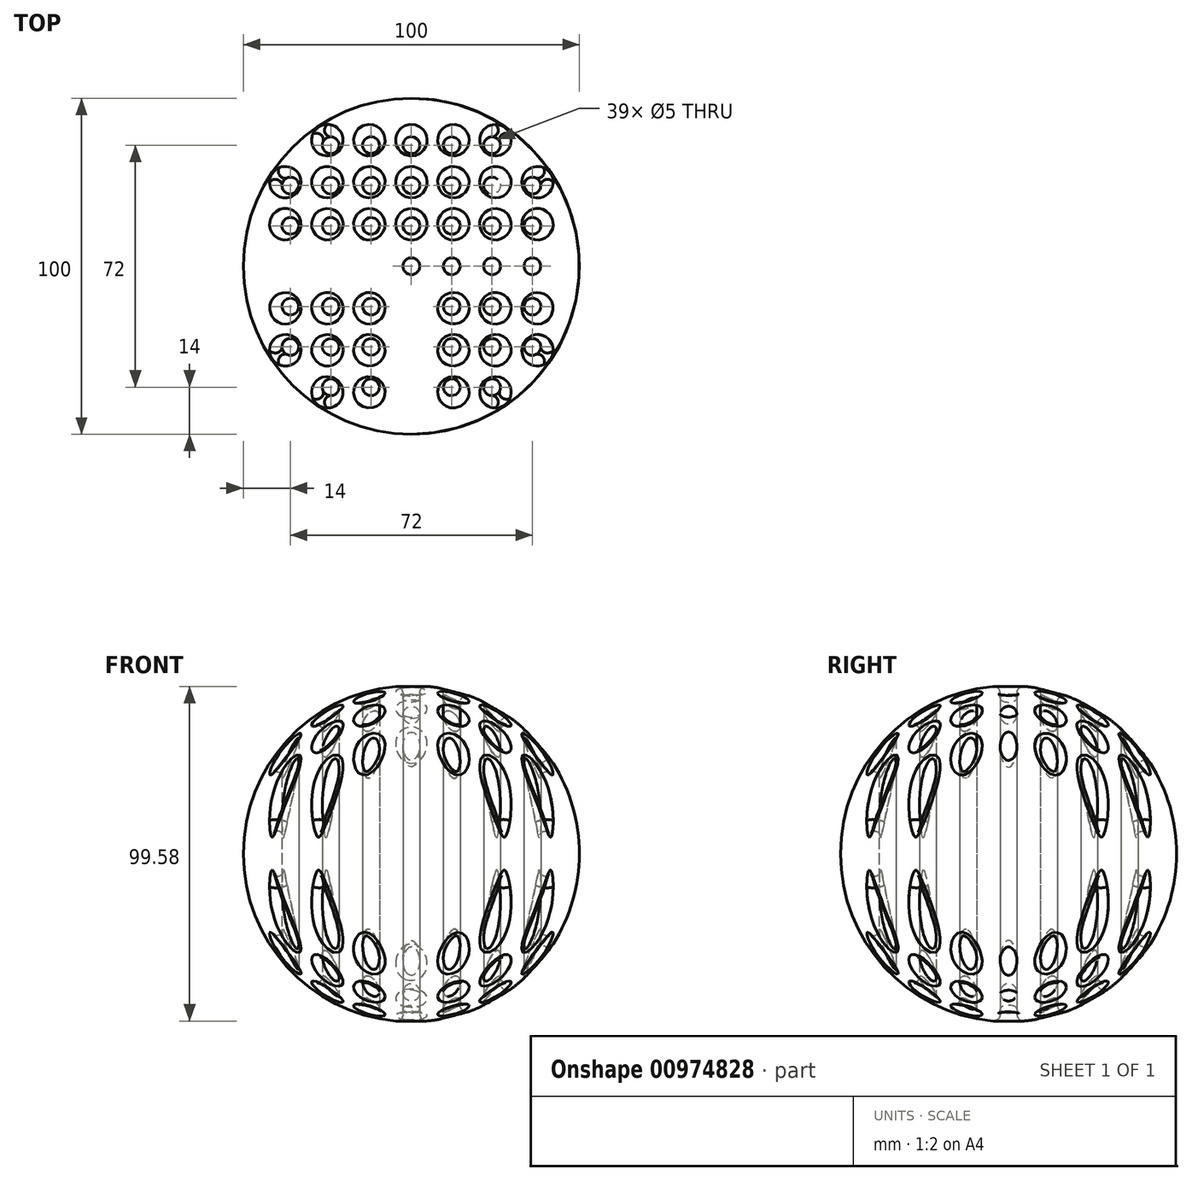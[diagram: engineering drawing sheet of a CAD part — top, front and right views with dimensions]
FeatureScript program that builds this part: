
annotation { "Feature Type Name" : "Feature", "Feature Type Description" : "" }
export const myFeature = defineFeature(function(context is Context, id is Id, definition is map)
    precondition{}
    {
        {
            var Q0;
            Q0=qCreatedBy(makeId("Top.planeOp"),FACE);
            var sketch = newSketch(context, id + "F0", { "sketchPlane" : qUnion([Q0])});
            skCircle(sketch, "E0", {"center": v(0, 0) * mm, "radius": 50 * mm});
            skLineSegment(sketch, "E1", {"start": v(0, 50) * mm, "end": v(0, 0) * mm});
            skLineSegment(sketch, "E2", {"start": v(0, 0) * mm, "end": v(0, -50) * mm});
            skSolve(sketch);
        }
        {
            var Q0;
            {var subQ0=sQuery(id+"F0.wireOp",EDGE,"E1");Q0=makeQuery(id+"F0.imprint","IMPRINT",FACE,{"disambiguationData":[TD([[makeQuery(id+"F0.imprint","IMPRINT",EDGE,{"derivedFrom":subQ0}),1.0]])]});}
            var Q1;
            Q1=sQuery(id+"F0.wireOp",EDGE,"E1");
            revolve(context, id + "F1", {"surfaceOperationType" : NewSurfaceOperationType.NEW, "entities" : qUnion([Q0]), "axis" : qUnion([Q1]), "revolveType" : RevolveType.FULL});
        }
        {
            var Q0;
            Q0=qCreatedBy(makeId("Top.planeOp"),FACE);
            var sketch = newSketch(context, id + "F2", { "sketchPlane" : qUnion([Q0])});
            skCircle(sketch, "E3", {"center": v(0, 0) * mm, "radius": 2.5 * mm});
            skCircle(sketch, "E4", {"center": v(0, 0) * mm, "radius": 50 * mm, "construction": true});
            skCircle(sketch, "E5.0.1.0", {"center": v(0, 12) * mm, "radius": 2.5 * mm});
            skCircle(sketch, "E5.0.2.0", {"center": v(0, 24) * mm, "radius": 2.5 * mm});
            skCircle(sketch, "E5.0.3.0", {"center": v(0, 36) * mm, "radius": 2.5 * mm});
            skCircle(sketch, "E5.1.0.0", {"center": v(12, 0) * mm, "radius": 2.5 * mm});
            skCircle(sketch, "E5.1.1.0", {"center": v(12, 12) * mm, "radius": 2.5 * mm});
            skCircle(sketch, "E5.1.2.0", {"center": v(12, 24) * mm, "radius": 2.5 * mm});
            skCircle(sketch, "E5.1.3.0", {"center": v(12, 36) * mm, "radius": 2.5 * mm});
            skCircle(sketch, "E5.2.0.0", {"center": v(24, 0) * mm, "radius": 2.5 * mm});
            skCircle(sketch, "E5.2.1.0", {"center": v(24, 12) * mm, "radius": 2.5 * mm});
            skCircle(sketch, "E5.2.2.0", {"center": v(24, 24) * mm, "radius": 2.5 * mm});
            skCircle(sketch, "E5.2.3.0", {"center": v(24, 36) * mm, "radius": 2.5 * mm});
            skCircle(sketch, "E5.3.0.0", {"center": v(36, 0) * mm, "radius": 2.5 * mm});
            skCircle(sketch, "E5.3.1.0", {"center": v(36, 12) * mm, "radius": 2.5 * mm});
            skCircle(sketch, "E5.3.2.0", {"center": v(36, 24) * mm, "radius": 2.5 * mm});
            skLineSegment(sketch, "E5.direction1", {"start": v(0, 0) * mm, "end": v(12, 0) * mm, "construction": true});
            skLineSegment(sketch, "E5.direction2", {"start": v(0, 0) * mm, "end": v(0, 12) * mm, "construction": true});
            skCircle(sketch, "E6.1.0", {"center": v(-12, 36) * mm, "radius": 2.5 * mm});
            skCircle(sketch, "E6.1.2", {"center": v(-24, 36) * mm, "radius": 2.5 * mm});
            skCircle(sketch, "E6.1.3", {"center": v(-12, 12) * mm, "radius": 2.5 * mm});
            skLineSegment(sketch, "E6.1.4", {"start": v(0, 0) * mm, "end": v(-12, 0) * mm, "construction": true});
            skCircle(sketch, "E6.1.5", {"center": v(-36, 12) * mm, "radius": 2.5 * mm});
            skCircle(sketch, "E6.1.6", {"center": v(-24, 12) * mm, "radius": 2.5 * mm});
            skCircle(sketch, "E6.1.8", {"center": v(-36, 0) * mm, "radius": 2.5 * mm});
            skCircle(sketch, "E6.1.9", {"center": v(-24, 24) * mm, "radius": 2.5 * mm});
            skCircle(sketch, "E6.1.10", {"center": v(-12, 24) * mm, "radius": 2.5 * mm});
            skCircle(sketch, "E6.1.12", {"center": v(-12, 0) * mm, "radius": 2.5 * mm});
            skCircle(sketch, "E6.1.13", {"center": v(-24, 0) * mm, "radius": 2.5 * mm});
            skCircle(sketch, "E6.1.15", {"center": v(-36, 24) * mm, "radius": 2.5 * mm});
            skCircle(sketch, "E6.2.0", {"center": v(-36, -12) * mm, "radius": 2.5 * mm});
            skCircle(sketch, "E6.2.1", {"center": v(-12, 0) * mm, "radius": 2.5 * mm});
            skCircle(sketch, "E6.2.2", {"center": v(-36, -24) * mm, "radius": 2.5 * mm});
            skCircle(sketch, "E6.2.3", {"center": v(-12, -12) * mm, "radius": 2.5 * mm});
            skLineSegment(sketch, "E6.2.4", {"start": v(0, 0) * mm, "end": v(0, -12) * mm, "construction": true});
            skCircle(sketch, "E6.2.5", {"center": v(-12, -36) * mm, "radius": 2.5 * mm});
            skCircle(sketch, "E6.2.6", {"center": v(-12, -24) * mm, "radius": 2.5 * mm});
            skCircle(sketch, "E6.2.8", {"center": v(0, -36) * mm, "radius": 2.5 * mm});
            skCircle(sketch, "E6.2.9", {"center": v(-24, -24) * mm, "radius": 2.5 * mm});
            skCircle(sketch, "E6.2.10", {"center": v(-24, -12) * mm, "radius": 2.5 * mm});
            skLineSegment(sketch, "E6.2.11", {"start": v(0, 0) * mm, "end": v(-12, 0) * mm, "construction": true});
            skCircle(sketch, "E6.2.12", {"center": v(0, -12) * mm, "radius": 2.5 * mm});
            skCircle(sketch, "E6.2.13", {"center": v(0, -24) * mm, "radius": 2.5 * mm});
            skCircle(sketch, "E6.2.14", {"center": v(-24, 0) * mm, "radius": 2.5 * mm});
            skCircle(sketch, "E6.2.15", {"center": v(-24, -36) * mm, "radius": 2.5 * mm});
            skCircle(sketch, "E6.2.16", {"center": v(-36, 0) * mm, "radius": 2.5 * mm});
            skCircle(sketch, "E6.3.0", {"center": v(12, -36) * mm, "radius": 2.5 * mm});
            skCircle(sketch, "E6.3.1", {"center": v(0, -12) * mm, "radius": 2.5 * mm});
            skCircle(sketch, "E6.3.2", {"center": v(24, -36) * mm, "radius": 2.5 * mm});
            skCircle(sketch, "E6.3.3", {"center": v(12, -12) * mm, "radius": 2.5 * mm});
            skCircle(sketch, "E6.3.5", {"center": v(36, -12) * mm, "radius": 2.5 * mm});
            skCircle(sketch, "E6.3.6", {"center": v(24, -12) * mm, "radius": 2.5 * mm});
            skCircle(sketch, "E6.3.9", {"center": v(24, -24) * mm, "radius": 2.5 * mm});
            skCircle(sketch, "E6.3.10", {"center": v(12, -24) * mm, "radius": 2.5 * mm});
            skLineSegment(sketch, "E6.3.11", {"start": v(0, 0) * mm, "end": v(0, -12) * mm, "construction": true});
            skCircle(sketch, "E6.3.14", {"center": v(0, -24) * mm, "radius": 2.5 * mm});
            skCircle(sketch, "E6.3.15", {"center": v(36, -24) * mm, "radius": 2.5 * mm});
            skCircle(sketch, "E6.3.16", {"center": v(0, -36) * mm, "radius": 2.5 * mm});
            skSolve(sketch);
        }
        {
            var Q0;
            Q0=makeQuery(id+"F2.imprint","IMPRINT",FACE,{"disambiguationData":[TD([[makeQuery(id+"F2.imprint","IMPRINT",EDGE,{"derivedFrom":sQuery(id+"F2.wireOp",EDGE,"E6.1.2")}),1.0]])]});
            var Q1;
            Q1=makeQuery(id+"F2.imprint","IMPRINT",FACE,{"disambiguationData":[TD([[makeQuery(id+"F2.imprint","IMPRINT",EDGE,{"derivedFrom":sQuery(id+"F2.wireOp",EDGE,"E6.1.0")}),1.0]])]});
            var Q2;
            Q2=makeQuery(id+"F2.imprint","IMPRINT",FACE,{"disambiguationData":[TD([[makeQuery(id+"F2.imprint","IMPRINT",EDGE,{"derivedFrom":sQuery(id+"F2.wireOp",EDGE,"E5.0.3.0")}),1.0]])]});
            var Q3;
            Q3=makeQuery(id+"F2.imprint","IMPRINT",FACE,{"disambiguationData":[TD([[makeQuery(id+"F2.imprint","IMPRINT",EDGE,{"derivedFrom":sQuery(id+"F2.wireOp",EDGE,"E5.1.3.0")}),1.0]])]});
            var Q4;
            Q4=makeQuery(id+"F2.imprint","IMPRINT",FACE,{"disambiguationData":[TD([[makeQuery(id+"F2.imprint","IMPRINT",EDGE,{"derivedFrom":sQuery(id+"F2.wireOp",EDGE,"E5.2.3.0")}),1.0]])]});
            var Q5;
            Q5=makeQuery(id+"F2.imprint","IMPRINT",FACE,{"disambiguationData":[TD([[makeQuery(id+"F2.imprint","IMPRINT",EDGE,{"derivedFrom":sQuery(id+"F2.wireOp",EDGE,"E5.2.2.0")}),1.0]])]});
            var Q6;
            Q6=makeQuery(id+"F2.imprint","IMPRINT",FACE,{"disambiguationData":[TD([[makeQuery(id+"F2.imprint","IMPRINT",EDGE,{"derivedFrom":sQuery(id+"F2.wireOp",EDGE,"E5.3.2.0")}),1.0]])]});
            var Q7;
            Q7=makeQuery(id+"F2.imprint","IMPRINT",FACE,{"disambiguationData":[TD([[makeQuery(id+"F2.imprint","IMPRINT",EDGE,{"derivedFrom":sQuery(id+"F2.wireOp",EDGE,"E5.1.2.0")}),1.0]])]});
            var Q8;
            Q8=makeQuery(id+"F2.imprint","IMPRINT",FACE,{"disambiguationData":[TD([[makeQuery(id+"F2.imprint","IMPRINT",EDGE,{"derivedFrom":sQuery(id+"F2.wireOp",EDGE,"E5.0.2.0")}),1.0]])]});
            var Q9;
            Q9=makeQuery(id+"F2.imprint","IMPRINT",FACE,{"disambiguationData":[TD([[makeQuery(id+"F2.imprint","IMPRINT",EDGE,{"derivedFrom":sQuery(id+"F2.wireOp",EDGE,"E6.1.10")}),1.0]])]});
            var Q10;
            Q10=makeQuery(id+"F2.imprint","IMPRINT",FACE,{"disambiguationData":[TD([[makeQuery(id+"F2.imprint","IMPRINT",EDGE,{"derivedFrom":sQuery(id+"F2.wireOp",EDGE,"E6.1.9")}),1.0]])]});
            var Q11;
            Q11=makeQuery(id+"F2.imprint","IMPRINT",FACE,{"disambiguationData":[TD([[makeQuery(id+"F2.imprint","IMPRINT",EDGE,{"derivedFrom":sQuery(id+"F2.wireOp",EDGE,"E6.1.15")}),1.0]])]});
            var Q12;
            Q12=makeQuery(id+"F2.imprint","IMPRINT",FACE,{"disambiguationData":[TD([[makeQuery(id+"F2.imprint","IMPRINT",EDGE,{"derivedFrom":sQuery(id+"F2.wireOp",EDGE,"E6.1.5")}),1.0]])]});
            var Q13;
            Q13=makeQuery(id+"F2.imprint","IMPRINT",FACE,{"disambiguationData":[TD([[makeQuery(id+"F2.imprint","IMPRINT",EDGE,{"derivedFrom":sQuery(id+"F2.wireOp",EDGE,"E6.1.6")}),1.0]])]});
            var Q14;
            Q14=makeQuery(id+"F2.imprint","IMPRINT",FACE,{"disambiguationData":[TD([[makeQuery(id+"F2.imprint","IMPRINT",EDGE,{"derivedFrom":sQuery(id+"F2.wireOp",EDGE,"E6.1.3")}),1.0]])]});
            var Q15;
            Q15=makeQuery(id+"F2.imprint","IMPRINT",FACE,{"disambiguationData":[TD([[makeQuery(id+"F2.imprint","IMPRINT",EDGE,{"derivedFrom":sQuery(id+"F2.wireOp",EDGE,"E5.0.1.0")}),1.0]])]});
            var Q16;
            Q16=makeQuery(id+"F2.imprint","IMPRINT",FACE,{"disambiguationData":[TD([[makeQuery(id+"F2.imprint","IMPRINT",EDGE,{"derivedFrom":sQuery(id+"F2.wireOp",EDGE,"E5.1.1.0")}),1.0]])]});
            var Q17;
            Q17=makeQuery(id+"F2.imprint","IMPRINT",FACE,{"disambiguationData":[TD([[makeQuery(id+"F2.imprint","IMPRINT",EDGE,{"derivedFrom":sQuery(id+"F2.wireOp",EDGE,"E5.2.1.0")}),1.0]])]});
            var Q18;
            Q18=makeQuery(id+"F2.imprint","IMPRINT",FACE,{"disambiguationData":[TD([[makeQuery(id+"F2.imprint","IMPRINT",EDGE,{"derivedFrom":sQuery(id+"F2.wireOp",EDGE,"E5.3.1.0")}),1.0]])]});
            var Q19;
            Q19=makeQuery(id+"F2.imprint","IMPRINT",FACE,{"disambiguationData":[TD([[makeQuery(id+"F2.imprint","IMPRINT",EDGE,{"derivedFrom":sQuery(id+"F2.wireOp",EDGE,"E5.3.0.0")}),1.0]])]});
            var Q20;
            Q20=makeQuery(id+"F2.imprint","IMPRINT",FACE,{"disambiguationData":[TD([[makeQuery(id+"F2.imprint","IMPRINT",EDGE,{"derivedFrom":sQuery(id+"F2.wireOp",EDGE,"E5.2.0.0")}),1.0]])]});
            var Q21;
            Q21=makeQuery(id+"F2.imprint","IMPRINT",FACE,{"disambiguationData":[TD([[makeQuery(id+"F2.imprint","IMPRINT",EDGE,{"derivedFrom":sQuery(id+"F2.wireOp",EDGE,"E5.1.0.0")}),1.0]])]});
            var Q22;
            Q22=makeQuery(id+"F2.imprint","IMPRINT",FACE,{"disambiguationData":[TD([[makeQuery(id+"F2.imprint","IMPRINT",EDGE,{"derivedFrom":sQuery(id+"F2.wireOp",EDGE,"E3")}),1.0]])]});
            var Q23;
            Q23=makeQuery(id+"F2.imprint","IMPRINT",FACE,{"disambiguationData":[TD([[makeQuery(id+"F2.imprint","IMPRINT",EDGE,{"derivedFrom":sQuery(id+"F2.wireOp",EDGE,"E6.2.1")}),1.0]])]});
            var Q24;
            Q24=makeQuery(id+"F2.imprint","IMPRINT",FACE,{"disambiguationData":[TD([[makeQuery(id+"F2.imprint","IMPRINT",EDGE,{"derivedFrom":sQuery(id+"F2.wireOp",EDGE,"E6.2.14")}),1.0]])]});
            var Q25;
            Q25=makeQuery(id+"F2.imprint","IMPRINT",FACE,{"disambiguationData":[TD([[makeQuery(id+"F2.imprint","IMPRINT",EDGE,{"derivedFrom":sQuery(id+"F2.wireOp",EDGE,"E6.2.16")}),1.0]])]});
            var Q26;
            Q26=makeQuery(id+"F2.imprint","IMPRINT",FACE,{"disambiguationData":[TD([[makeQuery(id+"F2.imprint","IMPRINT",EDGE,{"derivedFrom":sQuery(id+"F2.wireOp",EDGE,"E6.2.0")}),1.0]])]});
            var Q27;
            Q27=makeQuery(id+"F2.imprint","IMPRINT",FACE,{"disambiguationData":[TD([[makeQuery(id+"F2.imprint","IMPRINT",EDGE,{"derivedFrom":sQuery(id+"F2.wireOp",EDGE,"E6.2.10")}),1.0]])]});
            var Q28;
            Q28=makeQuery(id+"F2.imprint","IMPRINT",FACE,{"disambiguationData":[TD([[makeQuery(id+"F2.imprint","IMPRINT",EDGE,{"derivedFrom":sQuery(id+"F2.wireOp",EDGE,"E6.2.3")}),1.0]])]});
            var Q29;
            Q29=makeQuery(id+"F2.imprint","IMPRINT",FACE,{"disambiguationData":[TD([[makeQuery(id+"F2.imprint","IMPRINT",EDGE,{"derivedFrom":sQuery(id+"F2.wireOp",EDGE,"E6.3.1")}),1.0]])]});
            var Q30;
            Q30=makeQuery(id+"F2.imprint","IMPRINT",FACE,{"disambiguationData":[TD([[makeQuery(id+"F2.imprint","IMPRINT",EDGE,{"derivedFrom":sQuery(id+"F2.wireOp",EDGE,"E6.3.3")}),1.0]])]});
            var Q31;
            Q31=makeQuery(id+"F2.imprint","IMPRINT",FACE,{"disambiguationData":[TD([[makeQuery(id+"F2.imprint","IMPRINT",EDGE,{"derivedFrom":sQuery(id+"F2.wireOp",EDGE,"E6.3.6")}),1.0]])]});
            var Q32;
            Q32=makeQuery(id+"F2.imprint","IMPRINT",FACE,{"disambiguationData":[TD([[makeQuery(id+"F2.imprint","IMPRINT",EDGE,{"derivedFrom":sQuery(id+"F2.wireOp",EDGE,"E6.3.5")}),1.0]])]});
            var Q33;
            Q33=makeQuery(id+"F2.imprint","IMPRINT",FACE,{"disambiguationData":[TD([[makeQuery(id+"F2.imprint","IMPRINT",EDGE,{"derivedFrom":sQuery(id+"F2.wireOp",EDGE,"E6.2.2")}),1.0]])]});
            var Q34;
            Q34=makeQuery(id+"F2.imprint","IMPRINT",FACE,{"disambiguationData":[TD([[makeQuery(id+"F2.imprint","IMPRINT",EDGE,{"derivedFrom":sQuery(id+"F2.wireOp",EDGE,"E6.2.9")}),1.0]])]});
            var Q35;
            Q35=makeQuery(id+"F2.imprint","IMPRINT",FACE,{"disambiguationData":[TD([[makeQuery(id+"F2.imprint","IMPRINT",EDGE,{"derivedFrom":sQuery(id+"F2.wireOp",EDGE,"E6.2.6")}),1.0]])]});
            var Q36;
            Q36=makeQuery(id+"F2.imprint","IMPRINT",FACE,{"disambiguationData":[TD([[makeQuery(id+"F2.imprint","IMPRINT",EDGE,{"derivedFrom":sQuery(id+"F2.wireOp",EDGE,"E6.3.14")}),1.0]])]});
            var Q37;
            Q37=makeQuery(id+"F2.imprint","IMPRINT",FACE,{"disambiguationData":[TD([[makeQuery(id+"F2.imprint","IMPRINT",EDGE,{"derivedFrom":sQuery(id+"F2.wireOp",EDGE,"E6.3.10")}),1.0]])]});
            var Q38;
            Q38=makeQuery(id+"F2.imprint","IMPRINT",FACE,{"disambiguationData":[TD([[makeQuery(id+"F2.imprint","IMPRINT",EDGE,{"derivedFrom":sQuery(id+"F2.wireOp",EDGE,"E6.3.9")}),1.0]])]});
            var Q39;
            Q39=makeQuery(id+"F2.imprint","IMPRINT",FACE,{"disambiguationData":[TD([[makeQuery(id+"F2.imprint","IMPRINT",EDGE,{"derivedFrom":sQuery(id+"F2.wireOp",EDGE,"E6.3.15")}),1.0]])]});
            var Q40;
            Q40=makeQuery(id+"F2.imprint","IMPRINT",FACE,{"disambiguationData":[TD([[makeQuery(id+"F2.imprint","IMPRINT",EDGE,{"derivedFrom":sQuery(id+"F2.wireOp",EDGE,"E6.3.2")}),1.0]])]});
            var Q41;
            Q41=makeQuery(id+"F2.imprint","IMPRINT",FACE,{"disambiguationData":[TD([[makeQuery(id+"F2.imprint","IMPRINT",EDGE,{"derivedFrom":sQuery(id+"F2.wireOp",EDGE,"E6.3.0")}),1.0]])]});
            var Q42;
            Q42=makeQuery(id+"F2.imprint","IMPRINT",FACE,{"disambiguationData":[TD([[makeQuery(id+"F2.imprint","IMPRINT",EDGE,{"derivedFrom":sQuery(id+"F2.wireOp",EDGE,"E6.3.16")}),1.0]])]});
            var Q43;
            Q43=makeQuery(id+"F2.imprint","IMPRINT",FACE,{"disambiguationData":[TD([[makeQuery(id+"F2.imprint","IMPRINT",EDGE,{"derivedFrom":sQuery(id+"F2.wireOp",EDGE,"E6.2.5")}),1.0]])]});
            var Q44;
            Q44=makeQuery(id+"F2.imprint","IMPRINT",FACE,{"disambiguationData":[TD([[makeQuery(id+"F2.imprint","IMPRINT",EDGE,{"derivedFrom":sQuery(id+"F2.wireOp",EDGE,"E6.2.15")}),1.0]])]});
            extrude(context, id + "F3", {"entities" : qUnion([Q0, Q1, Q2, Q3, Q4, Q5, Q6, Q7, Q8, Q9, Q10, Q11, Q12, Q13, Q14, Q15, Q16, Q17, Q18, Q19, Q20, Q21, Q22, Q23, Q24, Q25, Q26, Q27, Q28, Q29, Q30, Q31, Q32, Q33, Q34, Q35, Q36, Q37, Q38, Q39, Q40, Q41, Q42, Q43, Q44]), "operationType" : NewBodyOperationType.REMOVE, "endBound" : BoundingType.SYMMETRIC, "depth" : 179 * mm, "offsetDistance" : 25 * mm});
        }
        {
            var Q0;
            Q0=makeQuery(id+"F3.boolean.opBoolean","INTERSECT",EDGE,{"disambiguationData":[OD(1.0)],"derivedFrom":[makeQuery(id+"F1.opRevolve","SWEPT_FACE",FACE,{"disambiguationData":[OSD([sQuery(id+"F0.wireOp",EDGE,"E0")])]}),makeQuery(id+"F3.opExtrude","SWEPT_FACE",FACE,{"disambiguationData":[OSD([sQuery(id+"F2.wireOp",EDGE,"E6.2.16")])]})]});
            var Q1;
            Q1=makeQuery(id+"F3.boolean.opBoolean","INTERSECT",EDGE,{"disambiguationData":[OD(1.0)],"derivedFrom":[makeQuery(id+"F1.opRevolve","SWEPT_FACE",FACE,{"disambiguationData":[OSD([sQuery(id+"F0.wireOp",EDGE,"E0")])]}),makeQuery(id+"F3.opExtrude","SWEPT_FACE",FACE,{"disambiguationData":[OSD([sQuery(id+"F2.wireOp",EDGE,"E6.2.2")])]})]});
            var Q2;
            Q2=makeQuery(id+"F3.boolean.opBoolean","INTERSECT",EDGE,{"disambiguationData":[OD(1.0)],"derivedFrom":[makeQuery(id+"F1.opRevolve","SWEPT_FACE",FACE,{"disambiguationData":[OSD([sQuery(id+"F0.wireOp",EDGE,"E0")])]}),makeQuery(id+"F3.opExtrude","SWEPT_FACE",FACE,{"disambiguationData":[OSD([sQuery(id+"F2.wireOp",EDGE,"E6.1.6")])]})]});
            var Q3;
            Q3=makeQuery(id+"F3.boolean.opBoolean","INTERSECT",EDGE,{"disambiguationData":[OD(1.0)],"derivedFrom":[makeQuery(id+"F1.opRevolve","SWEPT_FACE",FACE,{"disambiguationData":[OSD([sQuery(id+"F0.wireOp",EDGE,"E0")])]}),makeQuery(id+"F3.opExtrude","SWEPT_FACE",FACE,{"disambiguationData":[OSD([sQuery(id+"F2.wireOp",EDGE,"E6.3.16")])]})]});
            var Q4;
            Q4=makeQuery(id+"F3.boolean.opBoolean","INTERSECT",EDGE,{"disambiguationData":[OD(1.0)],"derivedFrom":[makeQuery(id+"F1.opRevolve","SWEPT_FACE",FACE,{"disambiguationData":[OSD([sQuery(id+"F0.wireOp",EDGE,"E0")])]}),makeQuery(id+"F3.opExtrude","SWEPT_FACE",FACE,{"disambiguationData":[OSD([sQuery(id+"F2.wireOp",EDGE,"E6.1.5")])]})]});
            var Q5;
            Q5=makeQuery(id+"F3.boolean.opBoolean","INTERSECT",EDGE,{"disambiguationData":[OD(1.0)],"derivedFrom":[makeQuery(id+"F1.opRevolve","SWEPT_FACE",FACE,{"disambiguationData":[OSD([sQuery(id+"F0.wireOp",EDGE,"E0")])]}),makeQuery(id+"F3.opExtrude","SWEPT_FACE",FACE,{"disambiguationData":[OSD([sQuery(id+"F2.wireOp",EDGE,"E6.2.1")])]})]});
            var Q6;
            Q6=makeQuery(id+"F3.boolean.opBoolean","INTERSECT",EDGE,{"disambiguationData":[OD(1.0)],"derivedFrom":[makeQuery(id+"F1.opRevolve","SWEPT_FACE",FACE,{"disambiguationData":[OSD([sQuery(id+"F0.wireOp",EDGE,"E0")])]}),makeQuery(id+"F3.opExtrude","SWEPT_FACE",FACE,{"disambiguationData":[OSD([sQuery(id+"F2.wireOp",EDGE,"E6.1.3")])]})]});
            var Q7;
            Q7=makeQuery(id+"F3.boolean.opBoolean","INTERSECT",EDGE,{"disambiguationData":[OD(1.0)],"derivedFrom":[makeQuery(id+"F1.opRevolve","SWEPT_FACE",FACE,{"disambiguationData":[OSD([sQuery(id+"F0.wireOp",EDGE,"E0")])]}),makeQuery(id+"F3.opExtrude","SWEPT_FACE",FACE,{"disambiguationData":[OSD([sQuery(id+"F2.wireOp",EDGE,"E6.3.14")])]})]});
            var Q8;
            Q8=makeQuery(id+"F3.boolean.opBoolean","INTERSECT",EDGE,{"disambiguationData":[OD(1.0)],"derivedFrom":[makeQuery(id+"F1.opRevolve","SWEPT_FACE",FACE,{"disambiguationData":[OSD([sQuery(id+"F0.wireOp",EDGE,"E0")])]}),makeQuery(id+"F3.opExtrude","SWEPT_FACE",FACE,{"disambiguationData":[OSD([sQuery(id+"F2.wireOp",EDGE,"E6.2.10")])]})]});
            var Q9;
            Q9=makeQuery(id+"F3.boolean.opBoolean","INTERSECT",EDGE,{"disambiguationData":[OD(1.0)],"derivedFrom":[makeQuery(id+"F1.opRevolve","SWEPT_FACE",FACE,{"disambiguationData":[OSD([sQuery(id+"F0.wireOp",EDGE,"E0")])]}),makeQuery(id+"F3.opExtrude","SWEPT_FACE",FACE,{"disambiguationData":[OSD([sQuery(id+"F2.wireOp",EDGE,"E6.3.5")])]})]});
            var Q10;
            Q10=makeQuery(id+"F3.boolean.opBoolean","INTERSECT",EDGE,{"disambiguationData":[OD(1.0)],"derivedFrom":[makeQuery(id+"F1.opRevolve","SWEPT_FACE",FACE,{"disambiguationData":[OSD([sQuery(id+"F0.wireOp",EDGE,"E0")])]}),makeQuery(id+"F3.opExtrude","SWEPT_FACE",FACE,{"disambiguationData":[OSD([sQuery(id+"F2.wireOp",EDGE,"E6.1.2")])]})]});
            var Q11;
            Q11=makeQuery(id+"F3.boolean.opBoolean","INTERSECT",EDGE,{"disambiguationData":[OD(1.0)],"derivedFrom":[makeQuery(id+"F1.opRevolve","SWEPT_FACE",FACE,{"disambiguationData":[OSD([sQuery(id+"F0.wireOp",EDGE,"E0")])]}),makeQuery(id+"F3.opExtrude","SWEPT_FACE",FACE,{"disambiguationData":[OSD([sQuery(id+"F2.wireOp",EDGE,"E5.0.3.0")])]})]});
            var Q12;
            Q12=makeQuery(id+"F3.boolean.opBoolean","INTERSECT",EDGE,{"disambiguationData":[OD(1.0)],"derivedFrom":[makeQuery(id+"F1.opRevolve","SWEPT_FACE",FACE,{"disambiguationData":[OSD([sQuery(id+"F0.wireOp",EDGE,"E0")])]}),makeQuery(id+"F3.opExtrude","SWEPT_FACE",FACE,{"disambiguationData":[OSD([sQuery(id+"F2.wireOp",EDGE,"E6.3.3")])]})]});
            var Q13;
            Q13=makeQuery(id+"F3.boolean.opBoolean","INTERSECT",EDGE,{"disambiguationData":[OD(1.0)],"derivedFrom":[makeQuery(id+"F1.opRevolve","SWEPT_FACE",FACE,{"disambiguationData":[OSD([sQuery(id+"F0.wireOp",EDGE,"E0")])]}),makeQuery(id+"F3.opExtrude","SWEPT_FACE",FACE,{"disambiguationData":[OSD([sQuery(id+"F2.wireOp",EDGE,"E5.2.0.0")])]})]});
            var Q14;
            Q14=makeQuery(id+"F3.boolean.opBoolean","INTERSECT",EDGE,{"disambiguationData":[OD(1.0)],"derivedFrom":[makeQuery(id+"F1.opRevolve","SWEPT_FACE",FACE,{"disambiguationData":[OSD([sQuery(id+"F0.wireOp",EDGE,"E0")])]}),makeQuery(id+"F3.opExtrude","SWEPT_FACE",FACE,{"disambiguationData":[OSD([sQuery(id+"F2.wireOp",EDGE,"E5.1.0.0")])]})]});
            var Q15;
            Q15=makeQuery(id+"F3.boolean.opBoolean","INTERSECT",EDGE,{"disambiguationData":[OD(1.0)],"derivedFrom":[makeQuery(id+"F1.opRevolve","SWEPT_FACE",FACE,{"disambiguationData":[OSD([sQuery(id+"F0.wireOp",EDGE,"E0")])]}),makeQuery(id+"F3.opExtrude","SWEPT_FACE",FACE,{"disambiguationData":[OSD([sQuery(id+"F2.wireOp",EDGE,"E6.2.6")])]})]});
            var Q16;
            Q16=makeQuery(id+"F3.boolean.opBoolean","INTERSECT",EDGE,{"disambiguationData":[OD(1.0)],"derivedFrom":[makeQuery(id+"F1.opRevolve","SWEPT_FACE",FACE,{"disambiguationData":[OSD([sQuery(id+"F0.wireOp",EDGE,"E0")])]}),makeQuery(id+"F3.opExtrude","SWEPT_FACE",FACE,{"disambiguationData":[OSD([sQuery(id+"F2.wireOp",EDGE,"E5.1.1.0")])]})]});
            var Q17;
            Q17=makeQuery(id+"F3.boolean.opBoolean","INTERSECT",EDGE,{"disambiguationData":[OD(1.0)],"derivedFrom":[makeQuery(id+"F1.opRevolve","SWEPT_FACE",FACE,{"disambiguationData":[OSD([sQuery(id+"F0.wireOp",EDGE,"E0")])]}),makeQuery(id+"F3.opExtrude","SWEPT_FACE",FACE,{"disambiguationData":[OSD([sQuery(id+"F2.wireOp",EDGE,"E6.1.9")])]})]});
            var Q18;
            Q18=makeQuery(id+"F3.boolean.opBoolean","INTERSECT",EDGE,{"disambiguationData":[OD(1.0)],"derivedFrom":[makeQuery(id+"F1.opRevolve","SWEPT_FACE",FACE,{"disambiguationData":[OSD([sQuery(id+"F0.wireOp",EDGE,"E0")])]}),makeQuery(id+"F3.opExtrude","SWEPT_FACE",FACE,{"disambiguationData":[OSD([sQuery(id+"F2.wireOp",EDGE,"E6.1.15")])]})]});
            var Q19;
            Q19=makeQuery(id+"F3.boolean.opBoolean","INTERSECT",EDGE,{"disambiguationData":[OD(1.0)],"derivedFrom":[makeQuery(id+"F1.opRevolve","SWEPT_FACE",FACE,{"disambiguationData":[OSD([sQuery(id+"F0.wireOp",EDGE,"E0")])]}),makeQuery(id+"F3.opExtrude","SWEPT_FACE",FACE,{"disambiguationData":[OSD([sQuery(id+"F2.wireOp",EDGE,"E6.2.15")])]})]});
            var Q20;
            Q20=makeQuery(id+"F3.boolean.opBoolean","INTERSECT",EDGE,{"disambiguationData":[OD(1.0)],"derivedFrom":[makeQuery(id+"F1.opRevolve","SWEPT_FACE",FACE,{"disambiguationData":[OSD([sQuery(id+"F0.wireOp",EDGE,"E0")])]}),makeQuery(id+"F3.opExtrude","SWEPT_FACE",FACE,{"disambiguationData":[OSD([sQuery(id+"F2.wireOp",EDGE,"E3")])]})]});
            var Q21;
            Q21=makeQuery(id+"F3.boolean.opBoolean","INTERSECT",EDGE,{"disambiguationData":[OD(1.0)],"derivedFrom":[makeQuery(id+"F1.opRevolve","SWEPT_FACE",FACE,{"disambiguationData":[OSD([sQuery(id+"F0.wireOp",EDGE,"E0")])]}),makeQuery(id+"F3.opExtrude","SWEPT_FACE",FACE,{"disambiguationData":[OSD([sQuery(id+"F2.wireOp",EDGE,"E6.3.1")])]})]});
            var Q22;
            Q22=makeQuery(id+"F3.boolean.opBoolean","INTERSECT",EDGE,{"disambiguationData":[OD(1.0)],"derivedFrom":[makeQuery(id+"F1.opRevolve","SWEPT_FACE",FACE,{"disambiguationData":[OSD([sQuery(id+"F0.wireOp",EDGE,"E0")])]}),makeQuery(id+"F3.opExtrude","SWEPT_FACE",FACE,{"disambiguationData":[OSD([sQuery(id+"F2.wireOp",EDGE,"E5.3.1.0")])]})]});
            var Q23;
            Q23=makeQuery(id+"F3.boolean.opBoolean","INTERSECT",EDGE,{"disambiguationData":[OD(1.0)],"derivedFrom":[makeQuery(id+"F1.opRevolve","SWEPT_FACE",FACE,{"disambiguationData":[OSD([sQuery(id+"F0.wireOp",EDGE,"E0")])]}),makeQuery(id+"F3.opExtrude","SWEPT_FACE",FACE,{"disambiguationData":[OSD([sQuery(id+"F2.wireOp",EDGE,"E5.2.1.0")])]})]});
            var Q24;
            Q24=makeQuery(id+"F3.boolean.opBoolean","INTERSECT",EDGE,{"disambiguationData":[OD(1.0)],"derivedFrom":[makeQuery(id+"F1.opRevolve","SWEPT_FACE",FACE,{"disambiguationData":[OSD([sQuery(id+"F0.wireOp",EDGE,"E0")])]}),makeQuery(id+"F3.opExtrude","SWEPT_FACE",FACE,{"disambiguationData":[OSD([sQuery(id+"F2.wireOp",EDGE,"E6.1.0")])]})]});
            var Q25;
            Q25=makeQuery(id+"F3.boolean.opBoolean","INTERSECT",EDGE,{"disambiguationData":[OD(1.0)],"derivedFrom":[makeQuery(id+"F1.opRevolve","SWEPT_FACE",FACE,{"disambiguationData":[OSD([sQuery(id+"F0.wireOp",EDGE,"E0")])]}),makeQuery(id+"F3.opExtrude","SWEPT_FACE",FACE,{"disambiguationData":[OSD([sQuery(id+"F2.wireOp",EDGE,"E5.0.2.0")])]})]});
            var Q26;
            Q26=makeQuery(id+"F3.boolean.opBoolean","INTERSECT",EDGE,{"disambiguationData":[OD(1.0)],"derivedFrom":[makeQuery(id+"F1.opRevolve","SWEPT_FACE",FACE,{"disambiguationData":[OSD([sQuery(id+"F0.wireOp",EDGE,"E0")])]}),makeQuery(id+"F3.opExtrude","SWEPT_FACE",FACE,{"disambiguationData":[OSD([sQuery(id+"F2.wireOp",EDGE,"E5.3.2.0")])]})]});
            var Q27;
            Q27=makeQuery(id+"F3.boolean.opBoolean","INTERSECT",EDGE,{"disambiguationData":[OD(1.0)],"derivedFrom":[makeQuery(id+"F1.opRevolve","SWEPT_FACE",FACE,{"disambiguationData":[OSD([sQuery(id+"F0.wireOp",EDGE,"E0")])]}),makeQuery(id+"F3.opExtrude","SWEPT_FACE",FACE,{"disambiguationData":[OSD([sQuery(id+"F2.wireOp",EDGE,"E5.0.1.0")])]})]});
            var Q28;
            Q28=makeQuery(id+"F3.boolean.opBoolean","INTERSECT",EDGE,{"disambiguationData":[OD(1.0)],"derivedFrom":[makeQuery(id+"F1.opRevolve","SWEPT_FACE",FACE,{"disambiguationData":[OSD([sQuery(id+"F0.wireOp",EDGE,"E0")])]}),makeQuery(id+"F3.opExtrude","SWEPT_FACE",FACE,{"disambiguationData":[OSD([sQuery(id+"F2.wireOp",EDGE,"E6.3.2")])]})]});
            var Q29;
            Q29=makeQuery(id+"F3.boolean.opBoolean","INTERSECT",EDGE,{"disambiguationData":[OD(1.0)],"derivedFrom":[makeQuery(id+"F1.opRevolve","SWEPT_FACE",FACE,{"disambiguationData":[OSD([sQuery(id+"F0.wireOp",EDGE,"E0")])]}),makeQuery(id+"F3.opExtrude","SWEPT_FACE",FACE,{"disambiguationData":[OSD([sQuery(id+"F2.wireOp",EDGE,"E6.3.6")])]})]});
            var Q30;
            Q30=makeQuery(id+"F3.boolean.opBoolean","INTERSECT",EDGE,{"disambiguationData":[OD(1.0)],"derivedFrom":[makeQuery(id+"F1.opRevolve","SWEPT_FACE",FACE,{"disambiguationData":[OSD([sQuery(id+"F0.wireOp",EDGE,"E0")])]}),makeQuery(id+"F3.opExtrude","SWEPT_FACE",FACE,{"disambiguationData":[OSD([sQuery(id+"F2.wireOp",EDGE,"E5.1.2.0")])]})]});
            var Q31;
            Q31=makeQuery(id+"F3.boolean.opBoolean","INTERSECT",EDGE,{"disambiguationData":[OD(1.0)],"derivedFrom":[makeQuery(id+"F1.opRevolve","SWEPT_FACE",FACE,{"disambiguationData":[OSD([sQuery(id+"F0.wireOp",EDGE,"E0")])]}),makeQuery(id+"F3.opExtrude","SWEPT_FACE",FACE,{"disambiguationData":[OSD([sQuery(id+"F2.wireOp",EDGE,"E5.1.3.0")])]})]});
            var Q32;
            Q32=makeQuery(id+"F3.boolean.opBoolean","INTERSECT",EDGE,{"disambiguationData":[OD(1.0)],"derivedFrom":[makeQuery(id+"F1.opRevolve","SWEPT_FACE",FACE,{"disambiguationData":[OSD([sQuery(id+"F0.wireOp",EDGE,"E0")])]}),makeQuery(id+"F3.opExtrude","SWEPT_FACE",FACE,{"disambiguationData":[OSD([sQuery(id+"F2.wireOp",EDGE,"E6.2.3")])]})]});
            var Q33;
            Q33=makeQuery(id+"F3.boolean.opBoolean","INTERSECT",EDGE,{"disambiguationData":[OD(1.0)],"derivedFrom":[makeQuery(id+"F1.opRevolve","SWEPT_FACE",FACE,{"disambiguationData":[OSD([sQuery(id+"F0.wireOp",EDGE,"E0")])]}),makeQuery(id+"F3.opExtrude","SWEPT_FACE",FACE,{"disambiguationData":[OSD([sQuery(id+"F2.wireOp",EDGE,"E6.2.9")])]})]});
            var Q34;
            Q34=makeQuery(id+"F3.boolean.opBoolean","INTERSECT",EDGE,{"disambiguationData":[OD(1.0)],"derivedFrom":[makeQuery(id+"F1.opRevolve","SWEPT_FACE",FACE,{"disambiguationData":[OSD([sQuery(id+"F0.wireOp",EDGE,"E0")])]}),makeQuery(id+"F3.opExtrude","SWEPT_FACE",FACE,{"disambiguationData":[OSD([sQuery(id+"F2.wireOp",EDGE,"E6.3.10")])]})]});
            var Q35;
            Q35=makeQuery(id+"F3.boolean.opBoolean","INTERSECT",EDGE,{"disambiguationData":[OD(1.0)],"derivedFrom":[makeQuery(id+"F1.opRevolve","SWEPT_FACE",FACE,{"disambiguationData":[OSD([sQuery(id+"F0.wireOp",EDGE,"E0")])]}),makeQuery(id+"F3.opExtrude","SWEPT_FACE",FACE,{"disambiguationData":[OSD([sQuery(id+"F2.wireOp",EDGE,"E6.2.0")])]})]});
            var Q36;
            Q36=makeQuery(id+"F3.boolean.opBoolean","INTERSECT",EDGE,{"disambiguationData":[OD(1.0)],"derivedFrom":[makeQuery(id+"F1.opRevolve","SWEPT_FACE",FACE,{"disambiguationData":[OSD([sQuery(id+"F0.wireOp",EDGE,"E0")])]}),makeQuery(id+"F3.opExtrude","SWEPT_FACE",FACE,{"disambiguationData":[OSD([sQuery(id+"F2.wireOp",EDGE,"E5.2.2.0")])]})]});
            var Q37;
            Q37=makeQuery(id+"F3.boolean.opBoolean","INTERSECT",EDGE,{"disambiguationData":[OD(1.0)],"derivedFrom":[makeQuery(id+"F1.opRevolve","SWEPT_FACE",FACE,{"disambiguationData":[OSD([sQuery(id+"F0.wireOp",EDGE,"E0")])]}),makeQuery(id+"F3.opExtrude","SWEPT_FACE",FACE,{"disambiguationData":[OSD([sQuery(id+"F2.wireOp",EDGE,"E5.2.3.0")])]})]});
            var Q38;
            Q38=makeQuery(id+"F3.boolean.opBoolean","INTERSECT",EDGE,{"disambiguationData":[OD(1.0)],"derivedFrom":[makeQuery(id+"F1.opRevolve","SWEPT_FACE",FACE,{"disambiguationData":[OSD([sQuery(id+"F0.wireOp",EDGE,"E0")])]}),makeQuery(id+"F3.opExtrude","SWEPT_FACE",FACE,{"disambiguationData":[OSD([sQuery(id+"F2.wireOp",EDGE,"E5.3.0.0")])]})]});
            var Q39;
            Q39=makeQuery(id+"F3.boolean.opBoolean","INTERSECT",EDGE,{"disambiguationData":[OD(1.0)],"derivedFrom":[makeQuery(id+"F1.opRevolve","SWEPT_FACE",FACE,{"disambiguationData":[OSD([sQuery(id+"F0.wireOp",EDGE,"E0")])]}),makeQuery(id+"F3.opExtrude","SWEPT_FACE",FACE,{"disambiguationData":[OSD([sQuery(id+"F2.wireOp",EDGE,"E6.2.14")])]})]});
            var Q40;
            Q40=makeQuery(id+"F3.boolean.opBoolean","INTERSECT",EDGE,{"disambiguationData":[OD(1.0)],"derivedFrom":[makeQuery(id+"F1.opRevolve","SWEPT_FACE",FACE,{"disambiguationData":[OSD([sQuery(id+"F0.wireOp",EDGE,"E0")])]}),makeQuery(id+"F3.opExtrude","SWEPT_FACE",FACE,{"disambiguationData":[OSD([sQuery(id+"F2.wireOp",EDGE,"E6.3.15")])]})]});
            var Q41;
            Q41=makeQuery(id+"F3.boolean.opBoolean","INTERSECT",EDGE,{"disambiguationData":[OD(1.0)],"derivedFrom":[makeQuery(id+"F1.opRevolve","SWEPT_FACE",FACE,{"disambiguationData":[OSD([sQuery(id+"F0.wireOp",EDGE,"E0")])]}),makeQuery(id+"F3.opExtrude","SWEPT_FACE",FACE,{"disambiguationData":[OSD([sQuery(id+"F2.wireOp",EDGE,"E6.1.10")])]})]});
            var Q42;
            Q42=makeQuery(id+"F3.boolean.opBoolean","INTERSECT",EDGE,{"disambiguationData":[OD(1.0)],"derivedFrom":[makeQuery(id+"F1.opRevolve","SWEPT_FACE",FACE,{"disambiguationData":[OSD([sQuery(id+"F0.wireOp",EDGE,"E0")])]}),makeQuery(id+"F3.opExtrude","SWEPT_FACE",FACE,{"disambiguationData":[OSD([sQuery(id+"F2.wireOp",EDGE,"E6.2.5")])]})]});
            var Q43;
            Q43=makeQuery(id+"F3.boolean.opBoolean","INTERSECT",EDGE,{"disambiguationData":[OD(1.0)],"derivedFrom":[makeQuery(id+"F1.opRevolve","SWEPT_FACE",FACE,{"disambiguationData":[OSD([sQuery(id+"F0.wireOp",EDGE,"E0")])]}),makeQuery(id+"F3.opExtrude","SWEPT_FACE",FACE,{"disambiguationData":[OSD([sQuery(id+"F2.wireOp",EDGE,"E6.3.9")])]})]});
            var Q44;
            Q44=makeQuery(id+"F3.boolean.opBoolean","INTERSECT",EDGE,{"disambiguationData":[OD(1.0)],"derivedFrom":[makeQuery(id+"F1.opRevolve","SWEPT_FACE",FACE,{"disambiguationData":[OSD([sQuery(id+"F0.wireOp",EDGE,"E0")])]}),makeQuery(id+"F3.opExtrude","SWEPT_FACE",FACE,{"disambiguationData":[OSD([sQuery(id+"F2.wireOp",EDGE,"E6.3.0")])]})]});
            fillet(context, id + "F4", {"entities" : qUnion([Q0, Q1, Q2, Q3, Q4, Q5, Q6, Q7, Q8, Q9, Q10, Q11, Q12, Q13, Q14, Q15, Q16, Q17, Q18, Q19, Q20, Q21, Q22, Q23, Q24, Q25, Q26, Q27, Q28, Q29, Q30, Q31, Q32, Q33, Q34, Q35, Q36, Q37, Q38, Q39, Q40, Q41, Q42, Q43, Q44]), "radius" : 2 * mm, "tangentPropagation" : true, "allowEdgeOverflow" : false});
        }
        {
            var Q0;
            Q0=makeQuery(id+"F3.boolean.opBoolean","INTERSECT",EDGE,{"disambiguationData":[OD(0.0)],"derivedFrom":[makeQuery(id+"F1.opRevolve","SWEPT_FACE",FACE,{"disambiguationData":[OSD([sQuery(id+"F0.wireOp",EDGE,"E0")])]}),makeQuery(id+"F3.opExtrude","SWEPT_FACE",FACE,{"disambiguationData":[OSD([sQuery(id+"F2.wireOp",EDGE,"E6.2.0")])]})]});
            var Q1;
            Q1=makeQuery(id+"F3.boolean.opBoolean","INTERSECT",EDGE,{"disambiguationData":[OD(0.0)],"derivedFrom":[makeQuery(id+"F1.opRevolve","SWEPT_FACE",FACE,{"disambiguationData":[OSD([sQuery(id+"F0.wireOp",EDGE,"E0")])]}),makeQuery(id+"F3.opExtrude","SWEPT_FACE",FACE,{"disambiguationData":[OSD([sQuery(id+"F2.wireOp",EDGE,"E6.3.3")])]})]});
            var Q2;
            Q2=makeQuery(id+"F3.boolean.opBoolean","INTERSECT",EDGE,{"disambiguationData":[OD(0.0)],"derivedFrom":[makeQuery(id+"F1.opRevolve","SWEPT_FACE",FACE,{"disambiguationData":[OSD([sQuery(id+"F0.wireOp",EDGE,"E0")])]}),makeQuery(id+"F3.opExtrude","SWEPT_FACE",FACE,{"disambiguationData":[OSD([sQuery(id+"F2.wireOp",EDGE,"E6.2.10")])]})]});
            var Q3;
            Q3=makeQuery(id+"F3.boolean.opBoolean","INTERSECT",EDGE,{"disambiguationData":[OD(0.0)],"derivedFrom":[makeQuery(id+"F1.opRevolve","SWEPT_FACE",FACE,{"disambiguationData":[OSD([sQuery(id+"F0.wireOp",EDGE,"E0")])]}),makeQuery(id+"F3.opExtrude","SWEPT_FACE",FACE,{"disambiguationData":[OSD([sQuery(id+"F2.wireOp",EDGE,"E5.2.0.0")])]})]});
            var Q4;
            Q4=makeQuery(id+"F3.boolean.opBoolean","INTERSECT",EDGE,{"disambiguationData":[OD(0.0)],"derivedFrom":[makeQuery(id+"F1.opRevolve","SWEPT_FACE",FACE,{"disambiguationData":[OSD([sQuery(id+"F0.wireOp",EDGE,"E0")])]}),makeQuery(id+"F3.opExtrude","SWEPT_FACE",FACE,{"disambiguationData":[OSD([sQuery(id+"F2.wireOp",EDGE,"E6.1.2")])]})]});
            var Q5;
            Q5=makeQuery(id+"F3.boolean.opBoolean","INTERSECT",EDGE,{"disambiguationData":[OD(0.0)],"derivedFrom":[makeQuery(id+"F1.opRevolve","SWEPT_FACE",FACE,{"disambiguationData":[OSD([sQuery(id+"F0.wireOp",EDGE,"E0")])]}),makeQuery(id+"F3.opExtrude","SWEPT_FACE",FACE,{"disambiguationData":[OSD([sQuery(id+"F2.wireOp",EDGE,"E6.2.5")])]})]});
            var Q6;
            Q6=makeQuery(id+"F3.boolean.opBoolean","INTERSECT",EDGE,{"disambiguationData":[OD(0.0)],"derivedFrom":[makeQuery(id+"F1.opRevolve","SWEPT_FACE",FACE,{"disambiguationData":[OSD([sQuery(id+"F0.wireOp",EDGE,"E0")])]}),makeQuery(id+"F3.opExtrude","SWEPT_FACE",FACE,{"disambiguationData":[OSD([sQuery(id+"F2.wireOp",EDGE,"E5.3.0.0")])]})]});
            var Q7;
            Q7=makeQuery(id+"F3.boolean.opBoolean","INTERSECT",EDGE,{"disambiguationData":[OD(0.0)],"derivedFrom":[makeQuery(id+"F1.opRevolve","SWEPT_FACE",FACE,{"disambiguationData":[OSD([sQuery(id+"F0.wireOp",EDGE,"E0")])]}),makeQuery(id+"F3.opExtrude","SWEPT_FACE",FACE,{"disambiguationData":[OSD([sQuery(id+"F2.wireOp",EDGE,"E6.2.2")])]})]});
            var Q8;
            Q8=makeQuery(id+"F3.boolean.opBoolean","INTERSECT",EDGE,{"disambiguationData":[OD(0.0)],"derivedFrom":[makeQuery(id+"F1.opRevolve","SWEPT_FACE",FACE,{"disambiguationData":[OSD([sQuery(id+"F0.wireOp",EDGE,"E0")])]}),makeQuery(id+"F3.opExtrude","SWEPT_FACE",FACE,{"disambiguationData":[OSD([sQuery(id+"F2.wireOp",EDGE,"E6.3.10")])]})]});
            var Q9;
            Q9=makeQuery(id+"F3.boolean.opBoolean","INTERSECT",EDGE,{"disambiguationData":[OD(1.0)],"derivedFrom":[makeQuery(id+"F1.opRevolve","SWEPT_FACE",FACE,{"disambiguationData":[OSD([sQuery(id+"F0.wireOp",EDGE,"E0")])]}),makeQuery(id+"F3.opExtrude","SWEPT_FACE",FACE,{"disambiguationData":[OSD([sQuery(id+"F2.wireOp",EDGE,"E6.2.15")])]})]});
            var Q10;
            Q10=makeQuery(id+"F3.boolean.opBoolean","INTERSECT",EDGE,{"disambiguationData":[OD(0.0)],"derivedFrom":[makeQuery(id+"F1.opRevolve","SWEPT_FACE",FACE,{"disambiguationData":[OSD([sQuery(id+"F0.wireOp",EDGE,"E0")])]}),makeQuery(id+"F3.opExtrude","SWEPT_FACE",FACE,{"disambiguationData":[OSD([sQuery(id+"F2.wireOp",EDGE,"E6.2.14")])]})]});
            var Q11;
            Q11=makeQuery(id+"F3.boolean.opBoolean","INTERSECT",EDGE,{"disambiguationData":[OD(0.0)],"derivedFrom":[makeQuery(id+"F1.opRevolve","SWEPT_FACE",FACE,{"disambiguationData":[OSD([sQuery(id+"F0.wireOp",EDGE,"E0")])]}),makeQuery(id+"F3.opExtrude","SWEPT_FACE",FACE,{"disambiguationData":[OSD([sQuery(id+"F2.wireOp",EDGE,"E5.2.2.0")])]})]});
            var Q12;
            Q12=makeQuery(id+"F3.boolean.opBoolean","INTERSECT",EDGE,{"disambiguationData":[OD(0.0)],"derivedFrom":[makeQuery(id+"F1.opRevolve","SWEPT_FACE",FACE,{"disambiguationData":[OSD([sQuery(id+"F0.wireOp",EDGE,"E0")])]}),makeQuery(id+"F3.opExtrude","SWEPT_FACE",FACE,{"disambiguationData":[OSD([sQuery(id+"F2.wireOp",EDGE,"E5.1.0.0")])]})]});
            var Q13;
            Q13=makeQuery(id+"F3.boolean.opBoolean","INTERSECT",EDGE,{"disambiguationData":[OD(0.0)],"derivedFrom":[makeQuery(id+"F1.opRevolve","SWEPT_FACE",FACE,{"disambiguationData":[OSD([sQuery(id+"F0.wireOp",EDGE,"E0")])]}),makeQuery(id+"F3.opExtrude","SWEPT_FACE",FACE,{"disambiguationData":[OSD([sQuery(id+"F2.wireOp",EDGE,"E6.2.1")])]})]});
            var Q14;
            Q14=makeQuery(id+"F3.boolean.opBoolean","INTERSECT",EDGE,{"disambiguationData":[OD(0.0)],"derivedFrom":[makeQuery(id+"F1.opRevolve","SWEPT_FACE",FACE,{"disambiguationData":[OSD([sQuery(id+"F0.wireOp",EDGE,"E0")])]}),makeQuery(id+"F3.opExtrude","SWEPT_FACE",FACE,{"disambiguationData":[OSD([sQuery(id+"F2.wireOp",EDGE,"E6.3.0")])]})]});
            var Q15;
            Q15=makeQuery(id+"F3.boolean.opBoolean","INTERSECT",EDGE,{"disambiguationData":[OD(0.0)],"derivedFrom":[makeQuery(id+"F1.opRevolve","SWEPT_FACE",FACE,{"disambiguationData":[OSD([sQuery(id+"F0.wireOp",EDGE,"E0")])]}),makeQuery(id+"F3.opExtrude","SWEPT_FACE",FACE,{"disambiguationData":[OSD([sQuery(id+"F2.wireOp",EDGE,"E6.2.3")])]})]});
            var Q16;
            Q16=makeQuery(id+"F3.boolean.opBoolean","INTERSECT",EDGE,{"disambiguationData":[OD(0.0)],"derivedFrom":[makeQuery(id+"F1.opRevolve","SWEPT_FACE",FACE,{"disambiguationData":[OSD([sQuery(id+"F0.wireOp",EDGE,"E0")])]}),makeQuery(id+"F3.opExtrude","SWEPT_FACE",FACE,{"disambiguationData":[OSD([sQuery(id+"F2.wireOp",EDGE,"E5.2.1.0")])]})]});
            var Q17;
            Q17=makeQuery(id+"F3.boolean.opBoolean","INTERSECT",EDGE,{"disambiguationData":[OD(0.0)],"derivedFrom":[makeQuery(id+"F1.opRevolve","SWEPT_FACE",FACE,{"disambiguationData":[OSD([sQuery(id+"F0.wireOp",EDGE,"E0")])]}),makeQuery(id+"F3.opExtrude","SWEPT_FACE",FACE,{"disambiguationData":[OSD([sQuery(id+"F2.wireOp",EDGE,"E6.1.10")])]})]});
            var Q18;
            Q18=makeQuery(id+"F3.boolean.opBoolean","INTERSECT",EDGE,{"disambiguationData":[OD(0.0)],"derivedFrom":[makeQuery(id+"F1.opRevolve","SWEPT_FACE",FACE,{"disambiguationData":[OSD([sQuery(id+"F0.wireOp",EDGE,"E0")])]}),makeQuery(id+"F3.opExtrude","SWEPT_FACE",FACE,{"disambiguationData":[OSD([sQuery(id+"F2.wireOp",EDGE,"E5.3.2.0")])]})]});
            var Q19;
            Q19=makeQuery(id+"F3.boolean.opBoolean","INTERSECT",EDGE,{"disambiguationData":[OD(0.0)],"derivedFrom":[makeQuery(id+"F1.opRevolve","SWEPT_FACE",FACE,{"disambiguationData":[OSD([sQuery(id+"F0.wireOp",EDGE,"E0")])]}),makeQuery(id+"F3.opExtrude","SWEPT_FACE",FACE,{"disambiguationData":[OSD([sQuery(id+"F2.wireOp",EDGE,"E6.3.1")])]})]});
            var Q20;
            Q20=makeQuery(id+"F3.boolean.opBoolean","INTERSECT",EDGE,{"disambiguationData":[OD(0.0)],"derivedFrom":[makeQuery(id+"F1.opRevolve","SWEPT_FACE",FACE,{"disambiguationData":[OSD([sQuery(id+"F0.wireOp",EDGE,"E0")])]}),makeQuery(id+"F3.opExtrude","SWEPT_FACE",FACE,{"disambiguationData":[OSD([sQuery(id+"F2.wireOp",EDGE,"E5.1.3.0")])]})]});
            var Q21;
            Q21=makeQuery(id+"F3.boolean.opBoolean","INTERSECT",EDGE,{"disambiguationData":[OD(0.0)],"derivedFrom":[makeQuery(id+"F1.opRevolve","SWEPT_FACE",FACE,{"disambiguationData":[OSD([sQuery(id+"F0.wireOp",EDGE,"E0")])]}),makeQuery(id+"F3.opExtrude","SWEPT_FACE",FACE,{"disambiguationData":[OSD([sQuery(id+"F2.wireOp",EDGE,"E6.1.15")])]})]});
            var Q22;
            Q22=makeQuery(id+"F3.boolean.opBoolean","INTERSECT",EDGE,{"disambiguationData":[OD(0.0)],"derivedFrom":[makeQuery(id+"F1.opRevolve","SWEPT_FACE",FACE,{"disambiguationData":[OSD([sQuery(id+"F0.wireOp",EDGE,"E0")])]}),makeQuery(id+"F3.opExtrude","SWEPT_FACE",FACE,{"disambiguationData":[OSD([sQuery(id+"F2.wireOp",EDGE,"E6.2.6")])]})]});
            var Q23;
            Q23=makeQuery(id+"F3.boolean.opBoolean","INTERSECT",EDGE,{"disambiguationData":[OD(0.0)],"derivedFrom":[makeQuery(id+"F1.opRevolve","SWEPT_FACE",FACE,{"disambiguationData":[OSD([sQuery(id+"F0.wireOp",EDGE,"E0")])]}),makeQuery(id+"F3.opExtrude","SWEPT_FACE",FACE,{"disambiguationData":[OSD([sQuery(id+"F2.wireOp",EDGE,"E5.3.1.0")])]})]});
            var Q24;
            Q24=makeQuery(id+"F3.boolean.opBoolean","INTERSECT",EDGE,{"disambiguationData":[OD(0.0)],"derivedFrom":[makeQuery(id+"F1.opRevolve","SWEPT_FACE",FACE,{"disambiguationData":[OSD([sQuery(id+"F0.wireOp",EDGE,"E0")])]}),makeQuery(id+"F3.opExtrude","SWEPT_FACE",FACE,{"disambiguationData":[OSD([sQuery(id+"F2.wireOp",EDGE,"E6.2.9")])]})]});
            var Q25;
            Q25=makeQuery(id+"F3.boolean.opBoolean","INTERSECT",EDGE,{"disambiguationData":[OD(0.0)],"derivedFrom":[makeQuery(id+"F1.opRevolve","SWEPT_FACE",FACE,{"disambiguationData":[OSD([sQuery(id+"F0.wireOp",EDGE,"E0")])]}),makeQuery(id+"F3.opExtrude","SWEPT_FACE",FACE,{"disambiguationData":[OSD([sQuery(id+"F2.wireOp",EDGE,"E5.0.2.0")])]})]});
            var Q26;
            Q26=makeQuery(id+"F3.boolean.opBoolean","INTERSECT",EDGE,{"disambiguationData":[OD(0.0)],"derivedFrom":[makeQuery(id+"F1.opRevolve","SWEPT_FACE",FACE,{"disambiguationData":[OSD([sQuery(id+"F0.wireOp",EDGE,"E0")])]}),makeQuery(id+"F3.opExtrude","SWEPT_FACE",FACE,{"disambiguationData":[OSD([sQuery(id+"F2.wireOp",EDGE,"E6.1.0")])]})]});
            var Q27;
            Q27=makeQuery(id+"F3.boolean.opBoolean","INTERSECT",EDGE,{"disambiguationData":[OD(0.0)],"derivedFrom":[makeQuery(id+"F1.opRevolve","SWEPT_FACE",FACE,{"disambiguationData":[OSD([sQuery(id+"F0.wireOp",EDGE,"E0")])]}),makeQuery(id+"F3.opExtrude","SWEPT_FACE",FACE,{"disambiguationData":[OSD([sQuery(id+"F2.wireOp",EDGE,"E6.3.6")])]})]});
            var Q28;
            Q28=makeQuery(id+"F3.boolean.opBoolean","INTERSECT",EDGE,{"disambiguationData":[OD(0.0)],"derivedFrom":[makeQuery(id+"F1.opRevolve","SWEPT_FACE",FACE,{"disambiguationData":[OSD([sQuery(id+"F0.wireOp",EDGE,"E0")])]}),makeQuery(id+"F3.opExtrude","SWEPT_FACE",FACE,{"disambiguationData":[OSD([sQuery(id+"F2.wireOp",EDGE,"E6.1.9")])]})]});
            var Q29;
            Q29=makeQuery(id+"F3.boolean.opBoolean","INTERSECT",EDGE,{"disambiguationData":[OD(0.0)],"derivedFrom":[makeQuery(id+"F1.opRevolve","SWEPT_FACE",FACE,{"disambiguationData":[OSD([sQuery(id+"F0.wireOp",EDGE,"E0")])]}),makeQuery(id+"F3.opExtrude","SWEPT_FACE",FACE,{"disambiguationData":[OSD([sQuery(id+"F2.wireOp",EDGE,"E6.1.3")])]})]});
            var Q30;
            Q30=makeQuery(id+"F3.boolean.opBoolean","INTERSECT",EDGE,{"disambiguationData":[OD(0.0)],"derivedFrom":[makeQuery(id+"F1.opRevolve","SWEPT_FACE",FACE,{"disambiguationData":[OSD([sQuery(id+"F0.wireOp",EDGE,"E0")])]}),makeQuery(id+"F3.opExtrude","SWEPT_FACE",FACE,{"disambiguationData":[OSD([sQuery(id+"F2.wireOp",EDGE,"E5.2.3.0")])]})]});
            var Q31;
            Q31=makeQuery(id+"F3.boolean.opBoolean","INTERSECT",EDGE,{"disambiguationData":[OD(0.0)],"derivedFrom":[makeQuery(id+"F1.opRevolve","SWEPT_FACE",FACE,{"disambiguationData":[OSD([sQuery(id+"F0.wireOp",EDGE,"E0")])]}),makeQuery(id+"F3.opExtrude","SWEPT_FACE",FACE,{"disambiguationData":[OSD([sQuery(id+"F2.wireOp",EDGE,"E6.3.5")])]})]});
            var Q32;
            Q32=makeQuery(id+"F3.boolean.opBoolean","INTERSECT",EDGE,{"disambiguationData":[OD(0.0)],"derivedFrom":[makeQuery(id+"F1.opRevolve","SWEPT_FACE",FACE,{"disambiguationData":[OSD([sQuery(id+"F0.wireOp",EDGE,"E0")])]}),makeQuery(id+"F3.opExtrude","SWEPT_FACE",FACE,{"disambiguationData":[OSD([sQuery(id+"F2.wireOp",EDGE,"E6.1.5")])]})]});
            var Q33;
            Q33=makeQuery(id+"F3.boolean.opBoolean","INTERSECT",EDGE,{"disambiguationData":[OD(0.0)],"derivedFrom":[makeQuery(id+"F1.opRevolve","SWEPT_FACE",FACE,{"disambiguationData":[OSD([sQuery(id+"F0.wireOp",EDGE,"E0")])]}),makeQuery(id+"F3.opExtrude","SWEPT_FACE",FACE,{"disambiguationData":[OSD([sQuery(id+"F2.wireOp",EDGE,"E6.3.16")])]})]});
            var Q34;
            Q34=makeQuery(id+"F3.boolean.opBoolean","INTERSECT",EDGE,{"disambiguationData":[OD(0.0)],"derivedFrom":[makeQuery(id+"F1.opRevolve","SWEPT_FACE",FACE,{"disambiguationData":[OSD([sQuery(id+"F0.wireOp",EDGE,"E0")])]}),makeQuery(id+"F3.opExtrude","SWEPT_FACE",FACE,{"disambiguationData":[OSD([sQuery(id+"F2.wireOp",EDGE,"E5.1.2.0")])]})]});
            var Q35;
            Q35=makeQuery(id+"F3.boolean.opBoolean","INTERSECT",EDGE,{"disambiguationData":[OD(0.0)],"derivedFrom":[makeQuery(id+"F1.opRevolve","SWEPT_FACE",FACE,{"disambiguationData":[OSD([sQuery(id+"F0.wireOp",EDGE,"E0")])]}),makeQuery(id+"F3.opExtrude","SWEPT_FACE",FACE,{"disambiguationData":[OSD([sQuery(id+"F2.wireOp",EDGE,"E5.1.1.0")])]})]});
            var Q36;
            Q36=makeQuery(id+"F3.boolean.opBoolean","INTERSECT",EDGE,{"disambiguationData":[OD(0.0)],"derivedFrom":[makeQuery(id+"F1.opRevolve","SWEPT_FACE",FACE,{"disambiguationData":[OSD([sQuery(id+"F0.wireOp",EDGE,"E0")])]}),makeQuery(id+"F3.opExtrude","SWEPT_FACE",FACE,{"disambiguationData":[OSD([sQuery(id+"F2.wireOp",EDGE,"E6.1.6")])]})]});
            var Q37;
            Q37=makeQuery(id+"F3.boolean.opBoolean","INTERSECT",EDGE,{"disambiguationData":[OD(0.0)],"derivedFrom":[makeQuery(id+"F1.opRevolve","SWEPT_FACE",FACE,{"disambiguationData":[OSD([sQuery(id+"F0.wireOp",EDGE,"E0")])]}),makeQuery(id+"F3.opExtrude","SWEPT_FACE",FACE,{"disambiguationData":[OSD([sQuery(id+"F2.wireOp",EDGE,"E6.2.16")])]})]});
            var Q38;
            Q38=makeQuery(id+"F3.boolean.opBoolean","INTERSECT",EDGE,{"disambiguationData":[OD(0.0)],"derivedFrom":[makeQuery(id+"F1.opRevolve","SWEPT_FACE",FACE,{"disambiguationData":[OSD([sQuery(id+"F0.wireOp",EDGE,"E0")])]}),makeQuery(id+"F3.opExtrude","SWEPT_FACE",FACE,{"disambiguationData":[OSD([sQuery(id+"F2.wireOp",EDGE,"E5.0.1.0")])]})]});
            var Q39;
            Q39=makeQuery(id+"F3.boolean.opBoolean","INTERSECT",EDGE,{"disambiguationData":[OD(0.0)],"derivedFrom":[makeQuery(id+"F1.opRevolve","SWEPT_FACE",FACE,{"disambiguationData":[OSD([sQuery(id+"F0.wireOp",EDGE,"E0")])]}),makeQuery(id+"F3.opExtrude","SWEPT_FACE",FACE,{"disambiguationData":[OSD([sQuery(id+"F2.wireOp",EDGE,"E6.3.2")])]})]});
            var Q40;
            Q40=makeQuery(id+"F3.boolean.opBoolean","INTERSECT",EDGE,{"disambiguationData":[OD(0.0)],"derivedFrom":[makeQuery(id+"F1.opRevolve","SWEPT_FACE",FACE,{"disambiguationData":[OSD([sQuery(id+"F0.wireOp",EDGE,"E0")])]}),makeQuery(id+"F3.opExtrude","SWEPT_FACE",FACE,{"disambiguationData":[OSD([sQuery(id+"F2.wireOp",EDGE,"E6.3.14")])]})]});
            var Q41;
            Q41=makeQuery(id+"F3.boolean.opBoolean","INTERSECT",EDGE,{"disambiguationData":[OD(0.0)],"derivedFrom":[makeQuery(id+"F1.opRevolve","SWEPT_FACE",FACE,{"disambiguationData":[OSD([sQuery(id+"F0.wireOp",EDGE,"E0")])]}),makeQuery(id+"F3.opExtrude","SWEPT_FACE",FACE,{"disambiguationData":[OSD([sQuery(id+"F2.wireOp",EDGE,"E6.2.15")])]})]});
            var Q42;
            Q42=makeQuery(id+"F3.boolean.opBoolean","INTERSECT",EDGE,{"disambiguationData":[OD(0.0)],"derivedFrom":[makeQuery(id+"F1.opRevolve","SWEPT_FACE",FACE,{"disambiguationData":[OSD([sQuery(id+"F0.wireOp",EDGE,"E0")])]}),makeQuery(id+"F3.opExtrude","SWEPT_FACE",FACE,{"disambiguationData":[OSD([sQuery(id+"F2.wireOp",EDGE,"E6.3.9")])]})]});
            var Q43;
            Q43=makeQuery(id+"F3.boolean.opBoolean","INTERSECT",EDGE,{"disambiguationData":[OD(0.0)],"derivedFrom":[makeQuery(id+"F1.opRevolve","SWEPT_FACE",FACE,{"disambiguationData":[OSD([sQuery(id+"F0.wireOp",EDGE,"E0")])]}),makeQuery(id+"F3.opExtrude","SWEPT_FACE",FACE,{"disambiguationData":[OSD([sQuery(id+"F2.wireOp",EDGE,"E6.3.15")])]})]});
            var Q44;
            Q44=makeQuery(id+"F3.boolean.opBoolean","INTERSECT",EDGE,{"disambiguationData":[OD(0.0)],"derivedFrom":[makeQuery(id+"F1.opRevolve","SWEPT_FACE",FACE,{"disambiguationData":[OSD([sQuery(id+"F0.wireOp",EDGE,"E0")])]}),makeQuery(id+"F3.opExtrude","SWEPT_FACE",FACE,{"disambiguationData":[OSD([sQuery(id+"F2.wireOp",EDGE,"E5.0.3.0")])]})]});
            var Q45;
            Q45=makeQuery(id+"F3.boolean.opBoolean","INTERSECT",EDGE,{"disambiguationData":[OD(1.0)],"derivedFrom":[makeQuery(id+"F1.opRevolve","SWEPT_FACE",FACE,{"disambiguationData":[OSD([sQuery(id+"F0.wireOp",EDGE,"E0")])]}),makeQuery(id+"F3.opExtrude","SWEPT_FACE",FACE,{"disambiguationData":[OSD([sQuery(id+"F2.wireOp",EDGE,"E6.2.16")])]})]});
            var Q46;
            Q46=makeQuery(id+"F3.boolean.opBoolean","INTERSECT",EDGE,{"disambiguationData":[OD(1.0)],"derivedFrom":[makeQuery(id+"F1.opRevolve","SWEPT_FACE",FACE,{"disambiguationData":[OSD([sQuery(id+"F0.wireOp",EDGE,"E0")])]}),makeQuery(id+"F3.opExtrude","SWEPT_FACE",FACE,{"disambiguationData":[OSD([sQuery(id+"F2.wireOp",EDGE,"E6.2.2")])]})]});
            var Q47;
            Q47=makeQuery(id+"F3.boolean.opBoolean","INTERSECT",EDGE,{"disambiguationData":[OD(1.0)],"derivedFrom":[makeQuery(id+"F1.opRevolve","SWEPT_FACE",FACE,{"disambiguationData":[OSD([sQuery(id+"F0.wireOp",EDGE,"E0")])]}),makeQuery(id+"F3.opExtrude","SWEPT_FACE",FACE,{"disambiguationData":[OSD([sQuery(id+"F2.wireOp",EDGE,"E6.1.6")])]})]});
            var Q48;
            Q48=makeQuery(id+"F3.boolean.opBoolean","INTERSECT",EDGE,{"disambiguationData":[OD(1.0)],"derivedFrom":[makeQuery(id+"F1.opRevolve","SWEPT_FACE",FACE,{"disambiguationData":[OSD([sQuery(id+"F0.wireOp",EDGE,"E0")])]}),makeQuery(id+"F3.opExtrude","SWEPT_FACE",FACE,{"disambiguationData":[OSD([sQuery(id+"F2.wireOp",EDGE,"E6.3.16")])]})]});
            var Q49;
            Q49=makeQuery(id+"F3.boolean.opBoolean","INTERSECT",EDGE,{"disambiguationData":[OD(1.0)],"derivedFrom":[makeQuery(id+"F1.opRevolve","SWEPT_FACE",FACE,{"disambiguationData":[OSD([sQuery(id+"F0.wireOp",EDGE,"E0")])]}),makeQuery(id+"F3.opExtrude","SWEPT_FACE",FACE,{"disambiguationData":[OSD([sQuery(id+"F2.wireOp",EDGE,"E6.1.5")])]})]});
            var Q50;
            Q50=makeQuery(id+"F3.boolean.opBoolean","INTERSECT",EDGE,{"disambiguationData":[OD(1.0)],"derivedFrom":[makeQuery(id+"F1.opRevolve","SWEPT_FACE",FACE,{"disambiguationData":[OSD([sQuery(id+"F0.wireOp",EDGE,"E0")])]}),makeQuery(id+"F3.opExtrude","SWEPT_FACE",FACE,{"disambiguationData":[OSD([sQuery(id+"F2.wireOp",EDGE,"E6.2.1")])]})]});
            var Q51;
            Q51=makeQuery(id+"F3.boolean.opBoolean","INTERSECT",EDGE,{"disambiguationData":[OD(1.0)],"derivedFrom":[makeQuery(id+"F1.opRevolve","SWEPT_FACE",FACE,{"disambiguationData":[OSD([sQuery(id+"F0.wireOp",EDGE,"E0")])]}),makeQuery(id+"F3.opExtrude","SWEPT_FACE",FACE,{"disambiguationData":[OSD([sQuery(id+"F2.wireOp",EDGE,"E6.1.3")])]})]});
            var Q52;
            Q52=makeQuery(id+"F3.boolean.opBoolean","INTERSECT",EDGE,{"disambiguationData":[OD(1.0)],"derivedFrom":[makeQuery(id+"F1.opRevolve","SWEPT_FACE",FACE,{"disambiguationData":[OSD([sQuery(id+"F0.wireOp",EDGE,"E0")])]}),makeQuery(id+"F3.opExtrude","SWEPT_FACE",FACE,{"disambiguationData":[OSD([sQuery(id+"F2.wireOp",EDGE,"E6.3.14")])]})]});
            var Q53;
            Q53=makeQuery(id+"F3.boolean.opBoolean","INTERSECT",EDGE,{"disambiguationData":[OD(1.0)],"derivedFrom":[makeQuery(id+"F1.opRevolve","SWEPT_FACE",FACE,{"disambiguationData":[OSD([sQuery(id+"F0.wireOp",EDGE,"E0")])]}),makeQuery(id+"F3.opExtrude","SWEPT_FACE",FACE,{"disambiguationData":[OSD([sQuery(id+"F2.wireOp",EDGE,"E6.2.10")])]})]});
            var Q54;
            Q54=makeQuery(id+"F3.boolean.opBoolean","INTERSECT",EDGE,{"disambiguationData":[OD(1.0)],"derivedFrom":[makeQuery(id+"F1.opRevolve","SWEPT_FACE",FACE,{"disambiguationData":[OSD([sQuery(id+"F0.wireOp",EDGE,"E0")])]}),makeQuery(id+"F3.opExtrude","SWEPT_FACE",FACE,{"disambiguationData":[OSD([sQuery(id+"F2.wireOp",EDGE,"E6.3.5")])]})]});
            var Q55;
            Q55=makeQuery(id+"F3.boolean.opBoolean","INTERSECT",EDGE,{"disambiguationData":[OD(1.0)],"derivedFrom":[makeQuery(id+"F1.opRevolve","SWEPT_FACE",FACE,{"disambiguationData":[OSD([sQuery(id+"F0.wireOp",EDGE,"E0")])]}),makeQuery(id+"F3.opExtrude","SWEPT_FACE",FACE,{"disambiguationData":[OSD([sQuery(id+"F2.wireOp",EDGE,"E6.1.2")])]})]});
            var Q56;
            Q56=makeQuery(id+"F3.boolean.opBoolean","INTERSECT",EDGE,{"disambiguationData":[OD(1.0)],"derivedFrom":[makeQuery(id+"F1.opRevolve","SWEPT_FACE",FACE,{"disambiguationData":[OSD([sQuery(id+"F0.wireOp",EDGE,"E0")])]}),makeQuery(id+"F3.opExtrude","SWEPT_FACE",FACE,{"disambiguationData":[OSD([sQuery(id+"F2.wireOp",EDGE,"E5.0.3.0")])]})]});
            var Q57;
            Q57=makeQuery(id+"F3.boolean.opBoolean","INTERSECT",EDGE,{"disambiguationData":[OD(1.0)],"derivedFrom":[makeQuery(id+"F1.opRevolve","SWEPT_FACE",FACE,{"disambiguationData":[OSD([sQuery(id+"F0.wireOp",EDGE,"E0")])]}),makeQuery(id+"F3.opExtrude","SWEPT_FACE",FACE,{"disambiguationData":[OSD([sQuery(id+"F2.wireOp",EDGE,"E6.3.3")])]})]});
            var Q58;
            Q58=makeQuery(id+"F3.boolean.opBoolean","INTERSECT",EDGE,{"disambiguationData":[OD(1.0)],"derivedFrom":[makeQuery(id+"F1.opRevolve","SWEPT_FACE",FACE,{"disambiguationData":[OSD([sQuery(id+"F0.wireOp",EDGE,"E0")])]}),makeQuery(id+"F3.opExtrude","SWEPT_FACE",FACE,{"disambiguationData":[OSD([sQuery(id+"F2.wireOp",EDGE,"E5.2.0.0")])]})]});
            var Q59;
            Q59=makeQuery(id+"F3.boolean.opBoolean","INTERSECT",EDGE,{"disambiguationData":[OD(1.0)],"derivedFrom":[makeQuery(id+"F1.opRevolve","SWEPT_FACE",FACE,{"disambiguationData":[OSD([sQuery(id+"F0.wireOp",EDGE,"E0")])]}),makeQuery(id+"F3.opExtrude","SWEPT_FACE",FACE,{"disambiguationData":[OSD([sQuery(id+"F2.wireOp",EDGE,"E5.1.0.0")])]})]});
            var Q60;
            Q60=makeQuery(id+"F3.boolean.opBoolean","INTERSECT",EDGE,{"disambiguationData":[OD(1.0)],"derivedFrom":[makeQuery(id+"F1.opRevolve","SWEPT_FACE",FACE,{"disambiguationData":[OSD([sQuery(id+"F0.wireOp",EDGE,"E0")])]}),makeQuery(id+"F3.opExtrude","SWEPT_FACE",FACE,{"disambiguationData":[OSD([sQuery(id+"F2.wireOp",EDGE,"E6.2.6")])]})]});
            var Q61;
            Q61=makeQuery(id+"F3.boolean.opBoolean","INTERSECT",EDGE,{"disambiguationData":[OD(1.0)],"derivedFrom":[makeQuery(id+"F1.opRevolve","SWEPT_FACE",FACE,{"disambiguationData":[OSD([sQuery(id+"F0.wireOp",EDGE,"E0")])]}),makeQuery(id+"F3.opExtrude","SWEPT_FACE",FACE,{"disambiguationData":[OSD([sQuery(id+"F2.wireOp",EDGE,"E5.1.1.0")])]})]});
            var Q62;
            Q62=makeQuery(id+"F3.boolean.opBoolean","INTERSECT",EDGE,{"disambiguationData":[OD(1.0)],"derivedFrom":[makeQuery(id+"F1.opRevolve","SWEPT_FACE",FACE,{"disambiguationData":[OSD([sQuery(id+"F0.wireOp",EDGE,"E0")])]}),makeQuery(id+"F3.opExtrude","SWEPT_FACE",FACE,{"disambiguationData":[OSD([sQuery(id+"F2.wireOp",EDGE,"E6.1.9")])]})]});
            var Q63;
            Q63=makeQuery(id+"F3.boolean.opBoolean","INTERSECT",EDGE,{"disambiguationData":[OD(1.0)],"derivedFrom":[makeQuery(id+"F1.opRevolve","SWEPT_FACE",FACE,{"disambiguationData":[OSD([sQuery(id+"F0.wireOp",EDGE,"E0")])]}),makeQuery(id+"F3.opExtrude","SWEPT_FACE",FACE,{"disambiguationData":[OSD([sQuery(id+"F2.wireOp",EDGE,"E6.1.15")])]})]});
            var Q64;
            Q64=makeQuery(id+"F3.boolean.opBoolean","INTERSECT",EDGE,{"disambiguationData":[OD(1.0)],"derivedFrom":[makeQuery(id+"F1.opRevolve","SWEPT_FACE",FACE,{"disambiguationData":[OSD([sQuery(id+"F0.wireOp",EDGE,"E0")])]}),makeQuery(id+"F3.opExtrude","SWEPT_FACE",FACE,{"disambiguationData":[OSD([sQuery(id+"F2.wireOp",EDGE,"E6.3.1")])]})]});
            var Q65;
            Q65=makeQuery(id+"F3.boolean.opBoolean","INTERSECT",EDGE,{"disambiguationData":[OD(1.0)],"derivedFrom":[makeQuery(id+"F1.opRevolve","SWEPT_FACE",FACE,{"disambiguationData":[OSD([sQuery(id+"F0.wireOp",EDGE,"E0")])]}),makeQuery(id+"F3.opExtrude","SWEPT_FACE",FACE,{"disambiguationData":[OSD([sQuery(id+"F2.wireOp",EDGE,"E5.3.1.0")])]})]});
            var Q66;
            Q66=makeQuery(id+"F3.boolean.opBoolean","INTERSECT",EDGE,{"disambiguationData":[OD(1.0)],"derivedFrom":[makeQuery(id+"F1.opRevolve","SWEPT_FACE",FACE,{"disambiguationData":[OSD([sQuery(id+"F0.wireOp",EDGE,"E0")])]}),makeQuery(id+"F3.opExtrude","SWEPT_FACE",FACE,{"disambiguationData":[OSD([sQuery(id+"F2.wireOp",EDGE,"E5.2.1.0")])]})]});
            var Q67;
            Q67=makeQuery(id+"F3.boolean.opBoolean","INTERSECT",EDGE,{"disambiguationData":[OD(1.0)],"derivedFrom":[makeQuery(id+"F1.opRevolve","SWEPT_FACE",FACE,{"disambiguationData":[OSD([sQuery(id+"F0.wireOp",EDGE,"E0")])]}),makeQuery(id+"F3.opExtrude","SWEPT_FACE",FACE,{"disambiguationData":[OSD([sQuery(id+"F2.wireOp",EDGE,"E6.1.0")])]})]});
            var Q68;
            Q68=makeQuery(id+"F3.boolean.opBoolean","INTERSECT",EDGE,{"disambiguationData":[OD(1.0)],"derivedFrom":[makeQuery(id+"F1.opRevolve","SWEPT_FACE",FACE,{"disambiguationData":[OSD([sQuery(id+"F0.wireOp",EDGE,"E0")])]}),makeQuery(id+"F3.opExtrude","SWEPT_FACE",FACE,{"disambiguationData":[OSD([sQuery(id+"F2.wireOp",EDGE,"E5.0.2.0")])]})]});
            var Q69;
            Q69=makeQuery(id+"F3.boolean.opBoolean","INTERSECT",EDGE,{"disambiguationData":[OD(1.0)],"derivedFrom":[makeQuery(id+"F1.opRevolve","SWEPT_FACE",FACE,{"disambiguationData":[OSD([sQuery(id+"F0.wireOp",EDGE,"E0")])]}),makeQuery(id+"F3.opExtrude","SWEPT_FACE",FACE,{"disambiguationData":[OSD([sQuery(id+"F2.wireOp",EDGE,"E5.3.2.0")])]})]});
            var Q70;
            Q70=makeQuery(id+"F3.boolean.opBoolean","INTERSECT",EDGE,{"disambiguationData":[OD(1.0)],"derivedFrom":[makeQuery(id+"F1.opRevolve","SWEPT_FACE",FACE,{"disambiguationData":[OSD([sQuery(id+"F0.wireOp",EDGE,"E0")])]}),makeQuery(id+"F3.opExtrude","SWEPT_FACE",FACE,{"disambiguationData":[OSD([sQuery(id+"F2.wireOp",EDGE,"E5.0.1.0")])]})]});
            var Q71;
            Q71=makeQuery(id+"F3.boolean.opBoolean","INTERSECT",EDGE,{"disambiguationData":[OD(1.0)],"derivedFrom":[makeQuery(id+"F1.opRevolve","SWEPT_FACE",FACE,{"disambiguationData":[OSD([sQuery(id+"F0.wireOp",EDGE,"E0")])]}),makeQuery(id+"F3.opExtrude","SWEPT_FACE",FACE,{"disambiguationData":[OSD([sQuery(id+"F2.wireOp",EDGE,"E6.3.2")])]})]});
            var Q72;
            Q72=makeQuery(id+"F3.boolean.opBoolean","INTERSECT",EDGE,{"disambiguationData":[OD(1.0)],"derivedFrom":[makeQuery(id+"F1.opRevolve","SWEPT_FACE",FACE,{"disambiguationData":[OSD([sQuery(id+"F0.wireOp",EDGE,"E0")])]}),makeQuery(id+"F3.opExtrude","SWEPT_FACE",FACE,{"disambiguationData":[OSD([sQuery(id+"F2.wireOp",EDGE,"E6.3.6")])]})]});
            var Q73;
            Q73=makeQuery(id+"F3.boolean.opBoolean","INTERSECT",EDGE,{"disambiguationData":[OD(1.0)],"derivedFrom":[makeQuery(id+"F1.opRevolve","SWEPT_FACE",FACE,{"disambiguationData":[OSD([sQuery(id+"F0.wireOp",EDGE,"E0")])]}),makeQuery(id+"F3.opExtrude","SWEPT_FACE",FACE,{"disambiguationData":[OSD([sQuery(id+"F2.wireOp",EDGE,"E5.1.2.0")])]})]});
            var Q74;
            Q74=makeQuery(id+"F3.boolean.opBoolean","INTERSECT",EDGE,{"disambiguationData":[OD(1.0)],"derivedFrom":[makeQuery(id+"F1.opRevolve","SWEPT_FACE",FACE,{"disambiguationData":[OSD([sQuery(id+"F0.wireOp",EDGE,"E0")])]}),makeQuery(id+"F3.opExtrude","SWEPT_FACE",FACE,{"disambiguationData":[OSD([sQuery(id+"F2.wireOp",EDGE,"E5.1.3.0")])]})]});
            var Q75;
            Q75=makeQuery(id+"F3.boolean.opBoolean","INTERSECT",EDGE,{"disambiguationData":[OD(1.0)],"derivedFrom":[makeQuery(id+"F1.opRevolve","SWEPT_FACE",FACE,{"disambiguationData":[OSD([sQuery(id+"F0.wireOp",EDGE,"E0")])]}),makeQuery(id+"F3.opExtrude","SWEPT_FACE",FACE,{"disambiguationData":[OSD([sQuery(id+"F2.wireOp",EDGE,"E6.2.3")])]})]});
            var Q76;
            Q76=makeQuery(id+"F3.boolean.opBoolean","INTERSECT",EDGE,{"disambiguationData":[OD(1.0)],"derivedFrom":[makeQuery(id+"F1.opRevolve","SWEPT_FACE",FACE,{"disambiguationData":[OSD([sQuery(id+"F0.wireOp",EDGE,"E0")])]}),makeQuery(id+"F3.opExtrude","SWEPT_FACE",FACE,{"disambiguationData":[OSD([sQuery(id+"F2.wireOp",EDGE,"E6.2.9")])]})]});
            var Q77;
            Q77=makeQuery(id+"F3.boolean.opBoolean","INTERSECT",EDGE,{"disambiguationData":[OD(1.0)],"derivedFrom":[makeQuery(id+"F1.opRevolve","SWEPT_FACE",FACE,{"disambiguationData":[OSD([sQuery(id+"F0.wireOp",EDGE,"E0")])]}),makeQuery(id+"F3.opExtrude","SWEPT_FACE",FACE,{"disambiguationData":[OSD([sQuery(id+"F2.wireOp",EDGE,"E6.3.10")])]})]});
            var Q78;
            Q78=makeQuery(id+"F3.boolean.opBoolean","INTERSECT",EDGE,{"disambiguationData":[OD(0.0)],"derivedFrom":[makeQuery(id+"F1.opRevolve","SWEPT_FACE",FACE,{"disambiguationData":[OSD([sQuery(id+"F0.wireOp",EDGE,"E0")])]}),makeQuery(id+"F3.opExtrude","SWEPT_FACE",FACE,{"disambiguationData":[OSD([sQuery(id+"F2.wireOp",EDGE,"E3")])]})]});
            var Q79;
            Q79=makeQuery(id+"F3.boolean.opBoolean","INTERSECT",EDGE,{"disambiguationData":[OD(1.0)],"derivedFrom":[makeQuery(id+"F1.opRevolve","SWEPT_FACE",FACE,{"disambiguationData":[OSD([sQuery(id+"F0.wireOp",EDGE,"E0")])]}),makeQuery(id+"F3.opExtrude","SWEPT_FACE",FACE,{"disambiguationData":[OSD([sQuery(id+"F2.wireOp",EDGE,"E6.2.0")])]})]});
            var Q80;
            Q80=makeQuery(id+"F3.boolean.opBoolean","INTERSECT",EDGE,{"disambiguationData":[OD(1.0)],"derivedFrom":[makeQuery(id+"F1.opRevolve","SWEPT_FACE",FACE,{"disambiguationData":[OSD([sQuery(id+"F0.wireOp",EDGE,"E0")])]}),makeQuery(id+"F3.opExtrude","SWEPT_FACE",FACE,{"disambiguationData":[OSD([sQuery(id+"F2.wireOp",EDGE,"E5.2.2.0")])]})]});
            var Q81;
            Q81=makeQuery(id+"F3.boolean.opBoolean","INTERSECT",EDGE,{"disambiguationData":[OD(1.0)],"derivedFrom":[makeQuery(id+"F1.opRevolve","SWEPT_FACE",FACE,{"disambiguationData":[OSD([sQuery(id+"F0.wireOp",EDGE,"E0")])]}),makeQuery(id+"F3.opExtrude","SWEPT_FACE",FACE,{"disambiguationData":[OSD([sQuery(id+"F2.wireOp",EDGE,"E5.2.3.0")])]})]});
            var Q82;
            Q82=makeQuery(id+"F3.boolean.opBoolean","INTERSECT",EDGE,{"disambiguationData":[OD(1.0)],"derivedFrom":[makeQuery(id+"F1.opRevolve","SWEPT_FACE",FACE,{"disambiguationData":[OSD([sQuery(id+"F0.wireOp",EDGE,"E0")])]}),makeQuery(id+"F3.opExtrude","SWEPT_FACE",FACE,{"disambiguationData":[OSD([sQuery(id+"F2.wireOp",EDGE,"E5.3.0.0")])]})]});
            var Q83;
            Q83=makeQuery(id+"F3.boolean.opBoolean","INTERSECT",EDGE,{"disambiguationData":[OD(1.0)],"derivedFrom":[makeQuery(id+"F1.opRevolve","SWEPT_FACE",FACE,{"disambiguationData":[OSD([sQuery(id+"F0.wireOp",EDGE,"E0")])]}),makeQuery(id+"F3.opExtrude","SWEPT_FACE",FACE,{"disambiguationData":[OSD([sQuery(id+"F2.wireOp",EDGE,"E6.2.14")])]})]});
            var Q84;
            Q84=makeQuery(id+"F3.boolean.opBoolean","INTERSECT",EDGE,{"disambiguationData":[OD(1.0)],"derivedFrom":[makeQuery(id+"F1.opRevolve","SWEPT_FACE",FACE,{"disambiguationData":[OSD([sQuery(id+"F0.wireOp",EDGE,"E0")])]}),makeQuery(id+"F3.opExtrude","SWEPT_FACE",FACE,{"disambiguationData":[OSD([sQuery(id+"F2.wireOp",EDGE,"E6.3.15")])]})]});
            var Q85;
            Q85=makeQuery(id+"F3.boolean.opBoolean","INTERSECT",EDGE,{"disambiguationData":[OD(1.0)],"derivedFrom":[makeQuery(id+"F1.opRevolve","SWEPT_FACE",FACE,{"disambiguationData":[OSD([sQuery(id+"F0.wireOp",EDGE,"E0")])]}),makeQuery(id+"F3.opExtrude","SWEPT_FACE",FACE,{"disambiguationData":[OSD([sQuery(id+"F2.wireOp",EDGE,"E6.1.10")])]})]});
            var Q86;
            Q86=makeQuery(id+"F3.boolean.opBoolean","INTERSECT",EDGE,{"disambiguationData":[OD(1.0)],"derivedFrom":[makeQuery(id+"F1.opRevolve","SWEPT_FACE",FACE,{"disambiguationData":[OSD([sQuery(id+"F0.wireOp",EDGE,"E0")])]}),makeQuery(id+"F3.opExtrude","SWEPT_FACE",FACE,{"disambiguationData":[OSD([sQuery(id+"F2.wireOp",EDGE,"E6.2.5")])]})]});
            var Q87;
            Q87=makeQuery(id+"F3.boolean.opBoolean","INTERSECT",EDGE,{"disambiguationData":[OD(1.0)],"derivedFrom":[makeQuery(id+"F1.opRevolve","SWEPT_FACE",FACE,{"disambiguationData":[OSD([sQuery(id+"F0.wireOp",EDGE,"E0")])]}),makeQuery(id+"F3.opExtrude","SWEPT_FACE",FACE,{"disambiguationData":[OSD([sQuery(id+"F2.wireOp",EDGE,"E6.3.9")])]})]});
            var Q88;
            Q88=makeQuery(id+"F3.boolean.opBoolean","INTERSECT",EDGE,{"disambiguationData":[OD(1.0)],"derivedFrom":[makeQuery(id+"F1.opRevolve","SWEPT_FACE",FACE,{"disambiguationData":[OSD([sQuery(id+"F0.wireOp",EDGE,"E0")])]}),makeQuery(id+"F3.opExtrude","SWEPT_FACE",FACE,{"disambiguationData":[OSD([sQuery(id+"F2.wireOp",EDGE,"E6.3.0")])]})]});
            var Q89;
            Q89=makeQuery(id+"F3.boolean.opBoolean","INTERSECT",EDGE,{"disambiguationData":[OD(1.0)],"derivedFrom":[makeQuery(id+"F1.opRevolve","SWEPT_FACE",FACE,{"disambiguationData":[OSD([sQuery(id+"F0.wireOp",EDGE,"E0")])]}),makeQuery(id+"F3.opExtrude","SWEPT_FACE",FACE,{"disambiguationData":[OSD([sQuery(id+"F2.wireOp",EDGE,"E3")])]})]});
            fillet(context, id + "F5", {"entities" : qUnion([Q0, Q1, Q2, Q3, Q4, Q5, Q6, Q7, Q8, Q9, Q10, Q11, Q12, Q13, Q14, Q15, Q16, Q17, Q18, Q19, Q20, Q21, Q22, Q23, Q24, Q25, Q26, Q27, Q28, Q29, Q30, Q31, Q32, Q33, Q34, Q35, Q36, Q37, Q38, Q39, Q40, Q41, Q42, Q43, Q44, Q45, Q46, Q47, Q48, Q49, Q50, Q51, Q52, Q53, Q54, Q55, Q56, Q57, Q58, Q59, Q60, Q61, Q62, Q63, Q64, Q65, Q66, Q67, Q68, Q69, Q70, Q71, Q72, Q73, Q74, Q75, Q76, Q77, Q78, Q79, Q80, Q81, Q82, Q83, Q84, Q85, Q86, Q87, Q88, Q89]), "radius" : 2 * mm, "tangentPropagation" : true, "allowEdgeOverflow" : false});
        }
    });
